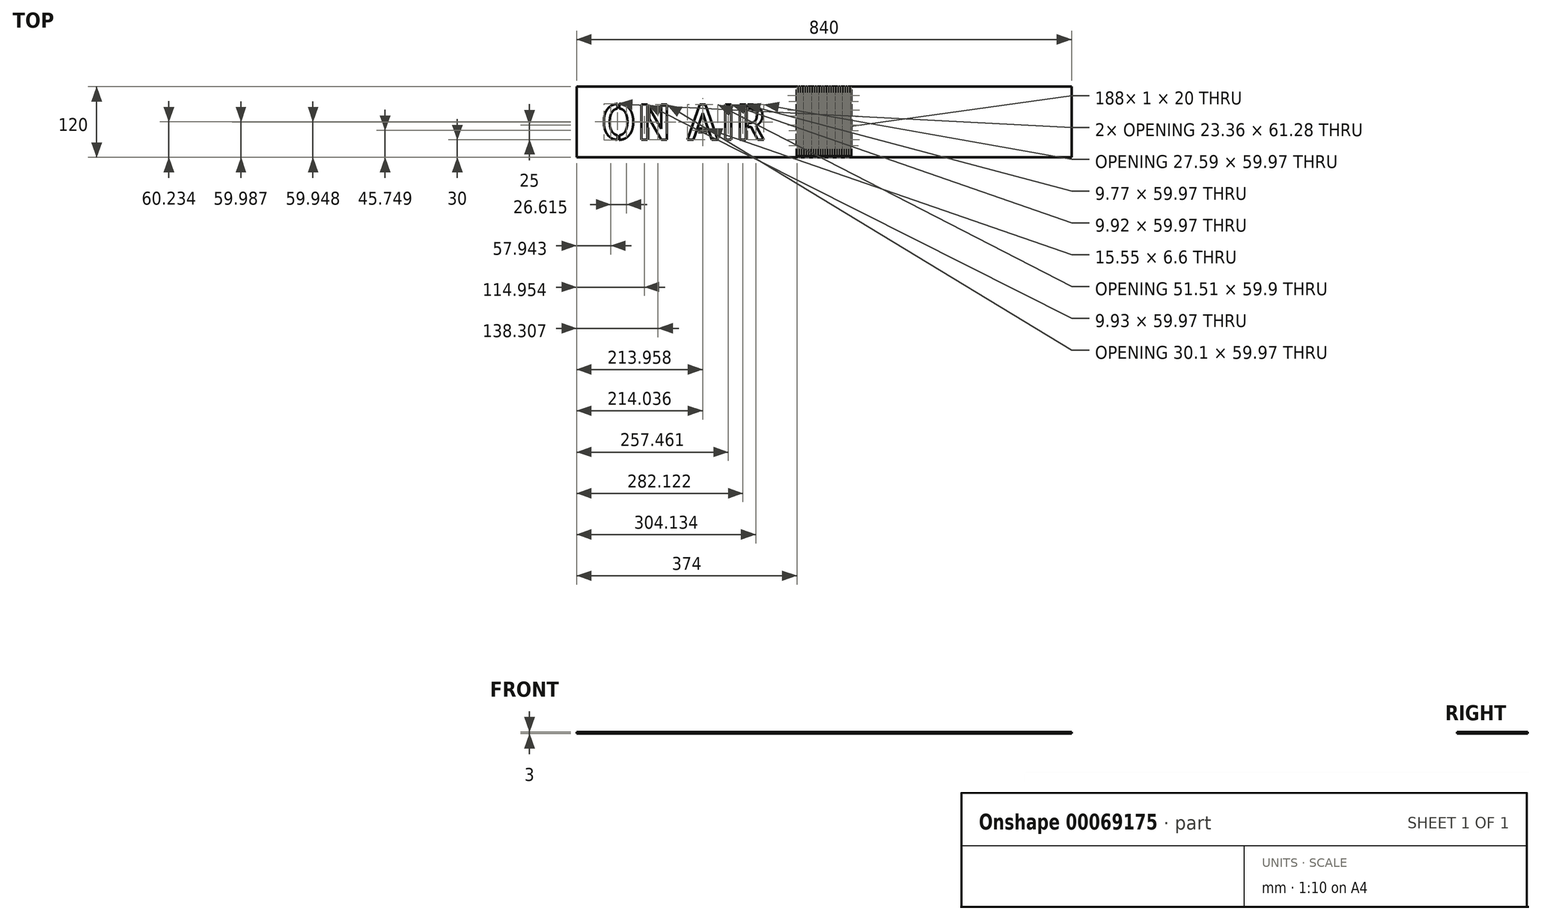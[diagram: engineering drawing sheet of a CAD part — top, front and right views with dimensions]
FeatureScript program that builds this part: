
annotation { "Feature Type Name" : "Feature", "Feature Type Description" : "" }
export const myFeature = defineFeature(function(context is Context, id is Id, definition is map)
    precondition{}
    {
        {
            var Q0;
            Q0=qCreatedBy(makeId("Top.planeOp"),FACE);
            var sketch = newSketch(context, id + "F0", { "sketchPlane" : qUnion([Q0])});
            skLineSegment(sketch, "E0", {"start": v(0, 120) * mm, "end": v(0, 0) * mm});
            skLineSegment(sketch, "E1", {"start": v(0, 0) * mm, "end": v(840, 0) * mm});
            skLineSegment(sketch, "E2", {"start": v(840, 0) * mm, "end": v(840, 120) * mm});
            skLineSegment(sketch, "E3", {"start": v(840, 120) * mm, "end": v(0, 120) * mm});
            skLineSegment(sketch, "E4", {"start": v(420, 120) * mm, "end": v(420, 0) * mm, "construction": true});
            skText(sketch, "E5", { "text": "ON AIR", "fontName": "AllertaStencil-Regular.ttf"});
            skLineSegment(sketch, "E6", {"start": v(417.5, 115) * mm, "end": v(417.5, 95) * mm});
            skLineSegment(sketch, "E7", {"start": v(417.5, 95) * mm, "end": v(418.5, 95) * mm});
            skLineSegment(sketch, "E8", {"start": v(418.5, 95) * mm, "end": v(418.5, 115) * mm});
            skLineSegment(sketch, "E9", {"start": v(418.5, 115) * mm, "end": v(417.5, 115) * mm});
            skLineSegment(sketch, "E10", {"start": v(419.5, 130) * mm, "end": v(419.5, 110) * mm});
            skLineSegment(sketch, "E11", {"start": v(419.5, 110) * mm, "end": v(420.5, 110) * mm});
            skLineSegment(sketch, "E12", {"start": v(420.5, 110) * mm, "end": v(420.5, 130) * mm});
            skLineSegment(sketch, "E13", {"start": v(420.5, 130) * mm, "end": v(419.5, 130) * mm});
            skLineSegment(sketch, "E14", {"start": v(420, 130) * mm, "end": v(420, 110) * mm, "construction": true});
            skPoint(sketch, "E15", {"position": v(419.5, 120) * mm});
            skLineSegment(sketch, "E16.MirrorCS", {"start": v(421.5, 115) * mm, "end": v(422.5, 115) * mm});
            skLineSegment(sketch, "E17.MirrorCS", {"start": v(422.5, 95) * mm, "end": v(421.5, 95) * mm});
            skLineSegment(sketch, "E18.MirrorCS", {"start": v(422.5, 115) * mm, "end": v(422.5, 95) * mm});
            skLineSegment(sketch, "E19.MirrorCS", {"start": v(421.5, 95) * mm, "end": v(421.5, 115) * mm});
            skLineSegment(sketch, "E20.0.1.0", {"start": v(422.5, 90) * mm, "end": v(422.5, 70) * mm});
            skLineSegment(sketch, "E20.0.1.1", {"start": v(418.5, 70) * mm, "end": v(418.5, 90) * mm});
            skLineSegment(sketch, "E20.0.1.2", {"start": v(421.5, 70) * mm, "end": v(421.5, 90) * mm});
            skLineSegment(sketch, "E20.0.1.3", {"start": v(420, 105) * mm, "end": v(420, 85) * mm, "construction": true});
            skLineSegment(sketch, "E20.0.1.4", {"start": v(419.5, 105) * mm, "end": v(419.5, 85) * mm});
            skPoint(sketch, "E20.0.1.5", {"position": v(419.5, 95) * mm});
            skLineSegment(sketch, "E20.0.1.6", {"start": v(420.5, 85) * mm, "end": v(420.5, 105) * mm});
            skLineSegment(sketch, "E20.0.1.7", {"start": v(417.5, 90) * mm, "end": v(417.5, 70) * mm});
            skLineSegment(sketch, "E20.0.1.8", {"start": v(417.5, 70) * mm, "end": v(418.5, 70) * mm});
            skLineSegment(sketch, "E20.0.1.9", {"start": v(420.5, 105) * mm, "end": v(419.5, 105) * mm});
            skLineSegment(sketch, "E20.0.1.10", {"start": v(422.5, 70) * mm, "end": v(421.5, 70) * mm});
            skLineSegment(sketch, "E20.0.1.11", {"start": v(421.5, 90) * mm, "end": v(422.5, 90) * mm});
            skLineSegment(sketch, "E20.0.1.12", {"start": v(418.5, 90) * mm, "end": v(417.5, 90) * mm});
            skLineSegment(sketch, "E20.0.1.13", {"start": v(419.5, 85) * mm, "end": v(420.5, 85) * mm});
            skLineSegment(sketch, "E20.0.2.0", {"start": v(422.5, 65) * mm, "end": v(422.5, 45) * mm});
            skLineSegment(sketch, "E20.0.2.1", {"start": v(418.5, 45) * mm, "end": v(418.5, 65) * mm});
            skLineSegment(sketch, "E20.0.2.2", {"start": v(421.5, 45) * mm, "end": v(421.5, 65) * mm});
            skLineSegment(sketch, "E20.0.2.3", {"start": v(420, 80) * mm, "end": v(420, 60) * mm, "construction": true});
            skLineSegment(sketch, "E20.0.2.4", {"start": v(419.5, 80) * mm, "end": v(419.5, 60) * mm});
            skPoint(sketch, "E20.0.2.5", {"position": v(419.5, 70) * mm});
            skLineSegment(sketch, "E20.0.2.6", {"start": v(420.5, 60) * mm, "end": v(420.5, 80) * mm});
            skLineSegment(sketch, "E20.0.2.7", {"start": v(417.5, 65) * mm, "end": v(417.5, 45) * mm});
            skLineSegment(sketch, "E20.0.2.8", {"start": v(417.5, 45) * mm, "end": v(418.5, 45) * mm});
            skLineSegment(sketch, "E20.0.2.9", {"start": v(420.5, 80) * mm, "end": v(419.5, 80) * mm});
            skLineSegment(sketch, "E20.0.2.10", {"start": v(422.5, 45) * mm, "end": v(421.5, 45) * mm});
            skLineSegment(sketch, "E20.0.2.11", {"start": v(421.5, 65) * mm, "end": v(422.5, 65) * mm});
            skLineSegment(sketch, "E20.0.2.12", {"start": v(418.5, 65) * mm, "end": v(417.5, 65) * mm});
            skLineSegment(sketch, "E20.0.2.13", {"start": v(419.5, 60) * mm, "end": v(420.5, 60) * mm});
            skLineSegment(sketch, "E20.0.3.0", {"start": v(422.5, 40) * mm, "end": v(422.5, 20) * mm});
            skLineSegment(sketch, "E20.0.3.1", {"start": v(418.5, 20) * mm, "end": v(418.5, 40) * mm});
            skLineSegment(sketch, "E20.0.3.2", {"start": v(421.5, 20) * mm, "end": v(421.5, 40) * mm});
            skLineSegment(sketch, "E20.0.3.3", {"start": v(420, 55) * mm, "end": v(420, 35) * mm, "construction": true});
            skLineSegment(sketch, "E20.0.3.4", {"start": v(419.5, 55) * mm, "end": v(419.5, 35) * mm});
            skPoint(sketch, "E20.0.3.5", {"position": v(419.5, 45) * mm});
            skLineSegment(sketch, "E20.0.3.6", {"start": v(420.5, 35) * mm, "end": v(420.5, 55) * mm});
            skLineSegment(sketch, "E20.0.3.7", {"start": v(417.5, 40) * mm, "end": v(417.5, 20) * mm});
            skLineSegment(sketch, "E20.0.3.8", {"start": v(417.5, 20) * mm, "end": v(418.5, 20) * mm});
            skLineSegment(sketch, "E20.0.3.9", {"start": v(420.5, 55) * mm, "end": v(419.5, 55) * mm});
            skLineSegment(sketch, "E20.0.3.10", {"start": v(422.5, 20) * mm, "end": v(421.5, 20) * mm});
            skLineSegment(sketch, "E20.0.3.11", {"start": v(421.5, 40) * mm, "end": v(422.5, 40) * mm});
            skLineSegment(sketch, "E20.0.3.12", {"start": v(418.5, 40) * mm, "end": v(417.5, 40) * mm});
            skLineSegment(sketch, "E20.0.3.13", {"start": v(419.5, 35) * mm, "end": v(420.5, 35) * mm});
            skLineSegment(sketch, "E20.0.4.0", {"start": v(422.5, 15) * mm, "end": v(422.5, -5) * mm});
            skLineSegment(sketch, "E20.0.4.1", {"start": v(418.5, -5) * mm, "end": v(418.5, 15) * mm});
            skLineSegment(sketch, "E20.0.4.2", {"start": v(421.5, -5) * mm, "end": v(421.5, 15) * mm});
            skLineSegment(sketch, "E20.0.4.3", {"start": v(420, 30) * mm, "end": v(420, 10) * mm, "construction": true});
            skLineSegment(sketch, "E20.0.4.4", {"start": v(419.5, 30) * mm, "end": v(419.5, 10) * mm});
            skPoint(sketch, "E20.0.4.5", {"position": v(419.5, 20) * mm});
            skLineSegment(sketch, "E20.0.4.6", {"start": v(420.5, 10) * mm, "end": v(420.5, 30) * mm});
            skLineSegment(sketch, "E20.0.4.7", {"start": v(417.5, 15) * mm, "end": v(417.5, -5) * mm});
            skLineSegment(sketch, "E20.0.4.8", {"start": v(417.5, -5) * mm, "end": v(418.5, -5) * mm});
            skLineSegment(sketch, "E20.0.4.9", {"start": v(420.5, 30) * mm, "end": v(419.5, 30) * mm});
            skLineSegment(sketch, "E20.0.4.10", {"start": v(422.5, -5) * mm, "end": v(421.5, -5) * mm});
            skLineSegment(sketch, "E20.0.4.11", {"start": v(421.5, 15) * mm, "end": v(422.5, 15) * mm});
            skLineSegment(sketch, "E20.0.4.12", {"start": v(418.5, 15) * mm, "end": v(417.5, 15) * mm});
            skLineSegment(sketch, "E20.0.4.13", {"start": v(419.5, 10) * mm, "end": v(420.5, 10) * mm});
            skLineSegment(sketch, "E20.0.5.0", {"start": v(422.5, -10) * mm, "end": v(422.5, -30) * mm});
            skLineSegment(sketch, "E20.0.5.1", {"start": v(418.5, -30) * mm, "end": v(418.5, -10) * mm});
            skLineSegment(sketch, "E20.0.5.2", {"start": v(421.5, -30) * mm, "end": v(421.5, -10) * mm});
            skLineSegment(sketch, "E20.0.5.3", {"start": v(420, 5) * mm, "end": v(420, -15) * mm, "construction": true});
            skLineSegment(sketch, "E20.0.5.4", {"start": v(419.5, 5) * mm, "end": v(419.5, -15) * mm});
            skPoint(sketch, "E20.0.5.5", {"position": v(419.5, -5) * mm});
            skLineSegment(sketch, "E20.0.5.6", {"start": v(420.5, -15) * mm, "end": v(420.5, 5) * mm});
            skLineSegment(sketch, "E20.0.5.7", {"start": v(417.5, -10) * mm, "end": v(417.5, -30) * mm});
            skLineSegment(sketch, "E20.0.5.8", {"start": v(417.5, -30) * mm, "end": v(418.5, -30) * mm});
            skLineSegment(sketch, "E20.0.5.9", {"start": v(420.5, 5) * mm, "end": v(419.5, 5) * mm});
            skLineSegment(sketch, "E20.0.5.10", {"start": v(422.5, -30) * mm, "end": v(421.5, -30) * mm});
            skLineSegment(sketch, "E20.0.5.11", {"start": v(421.5, -10) * mm, "end": v(422.5, -10) * mm});
            skLineSegment(sketch, "E20.0.5.12", {"start": v(418.5, -10) * mm, "end": v(417.5, -10) * mm});
            skLineSegment(sketch, "E20.0.5.13", {"start": v(419.5, -15) * mm, "end": v(420.5, -15) * mm});
            skLineSegment(sketch, "E20.direction1", {"start": v(422.5, 95) * mm, "end": v(422.5, 95) * mm});
            skLineSegment(sketch, "E20.direction2", {"start": v(422.5, 95) * mm, "end": v(422.5, 70) * mm, "construction": true});
            skLineSegment(sketch, "E21.1.0.0", {"start": v(426.5, -10) * mm, "end": v(426.5, -30) * mm});
            skPoint(sketch, "E21.1.0.1", {"position": v(423.5, 95) * mm});
            skLineSegment(sketch, "E21.1.0.2", {"start": v(425.5, 70) * mm, "end": v(425.5, 90) * mm});
            skLineSegment(sketch, "E21.1.0.3", {"start": v(425.5, 45) * mm, "end": v(425.5, 65) * mm});
            skLineSegment(sketch, "E21.1.0.4", {"start": v(426.5, 65) * mm, "end": v(426.5, 45) * mm});
            skPoint(sketch, "E21.1.0.5", {"position": v(423.5, 70) * mm});
            skLineSegment(sketch, "E21.1.0.6", {"start": v(425.5, -5) * mm, "end": v(425.5, 15) * mm});
            skPoint(sketch, "E21.1.0.7", {"position": v(423.5, 20) * mm});
            skLineSegment(sketch, "E21.1.0.8", {"start": v(426.5, 40) * mm, "end": v(426.5, 20) * mm});
            skLineSegment(sketch, "E21.1.0.9", {"start": v(425.5, -30) * mm, "end": v(425.5, -10) * mm});
            skPoint(sketch, "E21.1.0.10", {"position": v(423.5, 45) * mm});
            skLineSegment(sketch, "E21.1.0.11", {"start": v(425.5, 20) * mm, "end": v(425.5, 40) * mm});
            skLineSegment(sketch, "E21.1.0.12", {"start": v(426.5, 90) * mm, "end": v(426.5, 70) * mm});
            skLineSegment(sketch, "E21.1.0.13", {"start": v(426.5, 15) * mm, "end": v(426.5, -5) * mm});
            skPoint(sketch, "E21.1.0.14", {"position": v(423.5, -5) * mm});
            skLineSegment(sketch, "E21.1.0.15", {"start": v(424.5, 85) * mm, "end": v(424.5, 105) * mm});
            skLineSegment(sketch, "E21.1.0.16", {"start": v(426.5, 95) * mm, "end": v(426.5, 70) * mm, "construction": true});
            skLineSegment(sketch, "E21.1.0.17", {"start": v(424.5, 35) * mm, "end": v(424.5, 55) * mm});
            skLineSegment(sketch, "E21.1.0.18", {"start": v(424.5, 60) * mm, "end": v(424.5, 80) * mm});
            skLineSegment(sketch, "E21.1.0.19", {"start": v(424.5, -15) * mm, "end": v(424.5, 5) * mm});
            skLineSegment(sketch, "E21.1.0.20", {"start": v(423.5, 80) * mm, "end": v(423.5, 60) * mm});
            skLineSegment(sketch, "E21.1.0.21", {"start": v(425.5, 15) * mm, "end": v(426.5, 15) * mm});
            skLineSegment(sketch, "E21.1.0.22", {"start": v(423.5, 105) * mm, "end": v(423.5, 85) * mm});
            skLineSegment(sketch, "E21.1.0.23", {"start": v(423.5, 55) * mm, "end": v(423.5, 35) * mm});
            skLineSegment(sketch, "E21.1.0.24", {"start": v(425.5, -10) * mm, "end": v(426.5, -10) * mm});
            skLineSegment(sketch, "E21.1.0.25", {"start": v(424, 55) * mm, "end": v(424, 35) * mm, "construction": true});
            skLineSegment(sketch, "E21.1.0.26", {"start": v(426.5, -5) * mm, "end": v(425.5, -5) * mm});
            skLineSegment(sketch, "E21.1.0.27", {"start": v(423.5, 5) * mm, "end": v(423.5, -15) * mm});
            skLineSegment(sketch, "E21.1.0.28", {"start": v(424, 105) * mm, "end": v(424, 85) * mm, "construction": true});
            skLineSegment(sketch, "E21.1.0.29", {"start": v(424.5, 10) * mm, "end": v(424.5, 30) * mm});
            skLineSegment(sketch, "E21.1.0.30", {"start": v(425.5, 40) * mm, "end": v(426.5, 40) * mm});
            skLineSegment(sketch, "E21.1.0.31", {"start": v(424, 80) * mm, "end": v(424, 60) * mm, "construction": true});
            skLineSegment(sketch, "E21.1.0.32", {"start": v(424, 5) * mm, "end": v(424, -15) * mm, "construction": true});
            skLineSegment(sketch, "E21.1.0.33", {"start": v(426.5, -30) * mm, "end": v(425.5, -30) * mm});
            skLineSegment(sketch, "E21.1.0.34", {"start": v(423.5, 35) * mm, "end": v(424.5, 35) * mm});
            skLineSegment(sketch, "E21.1.0.35", {"start": v(426.5, 20) * mm, "end": v(425.5, 20) * mm});
            skLineSegment(sketch, "E21.1.0.36", {"start": v(426.5, 70) * mm, "end": v(425.5, 70) * mm});
            skLineSegment(sketch, "E21.1.0.37", {"start": v(423.5, -15) * mm, "end": v(424.5, -15) * mm});
            skLineSegment(sketch, "E21.1.0.38", {"start": v(424.5, 30) * mm, "end": v(423.5, 30) * mm});
            skLineSegment(sketch, "E21.1.0.39", {"start": v(424.5, 5) * mm, "end": v(423.5, 5) * mm});
            skLineSegment(sketch, "E21.1.0.40", {"start": v(423.5, 60) * mm, "end": v(424.5, 60) * mm});
            skLineSegment(sketch, "E21.1.0.41", {"start": v(424, 30) * mm, "end": v(424, 10) * mm, "construction": true});
            skLineSegment(sketch, "E21.1.0.42", {"start": v(425.5, 90) * mm, "end": v(426.5, 90) * mm});
            skLineSegment(sketch, "E21.1.0.43", {"start": v(424.5, 80) * mm, "end": v(423.5, 80) * mm});
            skLineSegment(sketch, "E21.1.0.44", {"start": v(423.5, 30) * mm, "end": v(423.5, 10) * mm});
            skLineSegment(sketch, "E21.1.0.45", {"start": v(424.5, 55) * mm, "end": v(423.5, 55) * mm});
            skLineSegment(sketch, "E21.1.0.46", {"start": v(423.5, 85) * mm, "end": v(424.5, 85) * mm});
            skLineSegment(sketch, "E21.1.0.47", {"start": v(423.5, 10) * mm, "end": v(424.5, 10) * mm});
            skLineSegment(sketch, "E21.1.0.48", {"start": v(425.5, 65) * mm, "end": v(426.5, 65) * mm});
            skLineSegment(sketch, "E21.1.0.49", {"start": v(426.5, 45) * mm, "end": v(425.5, 45) * mm});
            skLineSegment(sketch, "E21.1.0.50", {"start": v(425.5, 95) * mm, "end": v(425.5, 115) * mm});
            skLineSegment(sketch, "E21.1.0.51", {"start": v(426.5, 95) * mm, "end": v(425.5, 95) * mm});
            skLineSegment(sketch, "E21.1.0.52", {"start": v(426.5, 115) * mm, "end": v(426.5, 95) * mm});
            skLineSegment(sketch, "E21.1.0.53", {"start": v(425.5, 115) * mm, "end": v(426.5, 115) * mm});
            skLineSegment(sketch, "E21.1.0.54", {"start": v(424.5, 110) * mm, "end": v(424.5, 130) * mm});
            skLineSegment(sketch, "E21.1.0.55", {"start": v(423.5, 130) * mm, "end": v(423.5, 110) * mm});
            skLineSegment(sketch, "E21.1.0.56", {"start": v(423.5, 110) * mm, "end": v(424.5, 110) * mm});
            skLineSegment(sketch, "E21.1.0.57", {"start": v(424.5, 130) * mm, "end": v(423.5, 130) * mm});
            skLineSegment(sketch, "E21.2.0.0", {"start": v(430.5, -10) * mm, "end": v(430.5, -30) * mm});
            skPoint(sketch, "E21.2.0.1", {"position": v(427.5, 95) * mm});
            skLineSegment(sketch, "E21.2.0.2", {"start": v(429.5, 70) * mm, "end": v(429.5, 90) * mm});
            skLineSegment(sketch, "E21.2.0.3", {"start": v(429.5, 45) * mm, "end": v(429.5, 65) * mm});
            skLineSegment(sketch, "E21.2.0.4", {"start": v(430.5, 65) * mm, "end": v(430.5, 45) * mm});
            skPoint(sketch, "E21.2.0.5", {"position": v(427.5, 70) * mm});
            skLineSegment(sketch, "E21.2.0.6", {"start": v(429.5, -5) * mm, "end": v(429.5, 15) * mm});
            skPoint(sketch, "E21.2.0.7", {"position": v(427.5, 20) * mm});
            skLineSegment(sketch, "E21.2.0.8", {"start": v(430.5, 40) * mm, "end": v(430.5, 20) * mm});
            skLineSegment(sketch, "E21.2.0.9", {"start": v(429.5, -30) * mm, "end": v(429.5, -10) * mm});
            skPoint(sketch, "E21.2.0.10", {"position": v(427.5, 45) * mm});
            skLineSegment(sketch, "E21.2.0.11", {"start": v(429.5, 20) * mm, "end": v(429.5, 40) * mm});
            skLineSegment(sketch, "E21.2.0.12", {"start": v(430.5, 90) * mm, "end": v(430.5, 70) * mm});
            skLineSegment(sketch, "E21.2.0.13", {"start": v(430.5, 15) * mm, "end": v(430.5, -5) * mm});
            skPoint(sketch, "E21.2.0.14", {"position": v(427.5, -5) * mm});
            skLineSegment(sketch, "E21.2.0.15", {"start": v(428.5, 85) * mm, "end": v(428.5, 105) * mm});
            skLineSegment(sketch, "E21.2.0.16", {"start": v(430.5, 95) * mm, "end": v(430.5, 70) * mm, "construction": true});
            skLineSegment(sketch, "E21.2.0.17", {"start": v(428.5, 35) * mm, "end": v(428.5, 55) * mm});
            skLineSegment(sketch, "E21.2.0.18", {"start": v(428.5, 60) * mm, "end": v(428.5, 80) * mm});
            skLineSegment(sketch, "E21.2.0.19", {"start": v(428.5, -15) * mm, "end": v(428.5, 5) * mm});
            skLineSegment(sketch, "E21.2.0.20", {"start": v(427.5, 80) * mm, "end": v(427.5, 60) * mm});
            skLineSegment(sketch, "E21.2.0.21", {"start": v(429.5, 15) * mm, "end": v(430.5, 15) * mm});
            skLineSegment(sketch, "E21.2.0.22", {"start": v(427.5, 105) * mm, "end": v(427.5, 85) * mm});
            skLineSegment(sketch, "E21.2.0.23", {"start": v(427.5, 55) * mm, "end": v(427.5, 35) * mm});
            skLineSegment(sketch, "E21.2.0.24", {"start": v(429.5, -10) * mm, "end": v(430.5, -10) * mm});
            skLineSegment(sketch, "E21.2.0.25", {"start": v(428, 55) * mm, "end": v(428, 35) * mm, "construction": true});
            skLineSegment(sketch, "E21.2.0.26", {"start": v(430.5, -5) * mm, "end": v(429.5, -5) * mm});
            skLineSegment(sketch, "E21.2.0.27", {"start": v(427.5, 5) * mm, "end": v(427.5, -15) * mm});
            skLineSegment(sketch, "E21.2.0.28", {"start": v(428, 105) * mm, "end": v(428, 85) * mm, "construction": true});
            skLineSegment(sketch, "E21.2.0.29", {"start": v(428.5, 10) * mm, "end": v(428.5, 30) * mm});
            skLineSegment(sketch, "E21.2.0.30", {"start": v(429.5, 40) * mm, "end": v(430.5, 40) * mm});
            skLineSegment(sketch, "E21.2.0.31", {"start": v(428, 80) * mm, "end": v(428, 60) * mm, "construction": true});
            skLineSegment(sketch, "E21.2.0.32", {"start": v(428, 5) * mm, "end": v(428, -15) * mm, "construction": true});
            skLineSegment(sketch, "E21.2.0.33", {"start": v(430.5, -30) * mm, "end": v(429.5, -30) * mm});
            skLineSegment(sketch, "E21.2.0.34", {"start": v(427.5, 35) * mm, "end": v(428.5, 35) * mm});
            skLineSegment(sketch, "E21.2.0.35", {"start": v(430.5, 20) * mm, "end": v(429.5, 20) * mm});
            skLineSegment(sketch, "E21.2.0.36", {"start": v(430.5, 70) * mm, "end": v(429.5, 70) * mm});
            skLineSegment(sketch, "E21.2.0.37", {"start": v(427.5, -15) * mm, "end": v(428.5, -15) * mm});
            skLineSegment(sketch, "E21.2.0.38", {"start": v(428.5, 30) * mm, "end": v(427.5, 30) * mm});
            skLineSegment(sketch, "E21.2.0.39", {"start": v(428.5, 5) * mm, "end": v(427.5, 5) * mm});
            skLineSegment(sketch, "E21.2.0.40", {"start": v(427.5, 60) * mm, "end": v(428.5, 60) * mm});
            skLineSegment(sketch, "E21.2.0.41", {"start": v(428, 30) * mm, "end": v(428, 10) * mm, "construction": true});
            skLineSegment(sketch, "E21.2.0.42", {"start": v(429.5, 90) * mm, "end": v(430.5, 90) * mm});
            skLineSegment(sketch, "E21.2.0.43", {"start": v(428.5, 80) * mm, "end": v(427.5, 80) * mm});
            skLineSegment(sketch, "E21.2.0.44", {"start": v(427.5, 30) * mm, "end": v(427.5, 10) * mm});
            skLineSegment(sketch, "E21.2.0.45", {"start": v(428.5, 55) * mm, "end": v(427.5, 55) * mm});
            skLineSegment(sketch, "E21.2.0.46", {"start": v(427.5, 85) * mm, "end": v(428.5, 85) * mm});
            skLineSegment(sketch, "E21.2.0.47", {"start": v(427.5, 10) * mm, "end": v(428.5, 10) * mm});
            skLineSegment(sketch, "E21.2.0.48", {"start": v(429.5, 65) * mm, "end": v(430.5, 65) * mm});
            skLineSegment(sketch, "E21.2.0.49", {"start": v(430.5, 45) * mm, "end": v(429.5, 45) * mm});
            skLineSegment(sketch, "E21.2.0.50", {"start": v(429.5, 95) * mm, "end": v(429.5, 115) * mm});
            skLineSegment(sketch, "E21.2.0.51", {"start": v(430.5, 95) * mm, "end": v(429.5, 95) * mm});
            skLineSegment(sketch, "E21.2.0.52", {"start": v(430.5, 115) * mm, "end": v(430.5, 95) * mm});
            skLineSegment(sketch, "E21.2.0.53", {"start": v(429.5, 115) * mm, "end": v(430.5, 115) * mm});
            skLineSegment(sketch, "E21.2.0.54", {"start": v(428.5, 110) * mm, "end": v(428.5, 130) * mm});
            skLineSegment(sketch, "E21.2.0.55", {"start": v(427.5, 130) * mm, "end": v(427.5, 110) * mm});
            skLineSegment(sketch, "E21.2.0.56", {"start": v(427.5, 110) * mm, "end": v(428.5, 110) * mm});
            skLineSegment(sketch, "E21.2.0.57", {"start": v(428.5, 130) * mm, "end": v(427.5, 130) * mm});
            skLineSegment(sketch, "E21.3.0.0", {"start": v(434.5, -10) * mm, "end": v(434.5, -30) * mm});
            skPoint(sketch, "E21.3.0.1", {"position": v(431.5, 95) * mm});
            skLineSegment(sketch, "E21.3.0.2", {"start": v(433.5, 70) * mm, "end": v(433.5, 90) * mm});
            skLineSegment(sketch, "E21.3.0.3", {"start": v(433.5, 45) * mm, "end": v(433.5, 65) * mm});
            skLineSegment(sketch, "E21.3.0.4", {"start": v(434.5, 65) * mm, "end": v(434.5, 45) * mm});
            skPoint(sketch, "E21.3.0.5", {"position": v(431.5, 70) * mm});
            skLineSegment(sketch, "E21.3.0.6", {"start": v(433.5, -5) * mm, "end": v(433.5, 15) * mm});
            skPoint(sketch, "E21.3.0.7", {"position": v(431.5, 20) * mm});
            skLineSegment(sketch, "E21.3.0.8", {"start": v(434.5, 40) * mm, "end": v(434.5, 20) * mm});
            skLineSegment(sketch, "E21.3.0.9", {"start": v(433.5, -30) * mm, "end": v(433.5, -10) * mm});
            skPoint(sketch, "E21.3.0.10", {"position": v(431.5, 45) * mm});
            skLineSegment(sketch, "E21.3.0.11", {"start": v(433.5, 20) * mm, "end": v(433.5, 40) * mm});
            skLineSegment(sketch, "E21.3.0.12", {"start": v(434.5, 90) * mm, "end": v(434.5, 70) * mm});
            skLineSegment(sketch, "E21.3.0.13", {"start": v(434.5, 15) * mm, "end": v(434.5, -5) * mm});
            skPoint(sketch, "E21.3.0.14", {"position": v(431.5, -5) * mm});
            skLineSegment(sketch, "E21.3.0.15", {"start": v(432.5, 85) * mm, "end": v(432.5, 105) * mm});
            skLineSegment(sketch, "E21.3.0.16", {"start": v(434.5, 95) * mm, "end": v(434.5, 70) * mm, "construction": true});
            skLineSegment(sketch, "E21.3.0.17", {"start": v(432.5, 35) * mm, "end": v(432.5, 55) * mm});
            skLineSegment(sketch, "E21.3.0.18", {"start": v(432.5, 60) * mm, "end": v(432.5, 80) * mm});
            skLineSegment(sketch, "E21.3.0.19", {"start": v(432.5, -15) * mm, "end": v(432.5, 5) * mm});
            skLineSegment(sketch, "E21.3.0.20", {"start": v(431.5, 80) * mm, "end": v(431.5, 60) * mm});
            skLineSegment(sketch, "E21.3.0.21", {"start": v(433.5, 15) * mm, "end": v(434.5, 15) * mm});
            skLineSegment(sketch, "E21.3.0.22", {"start": v(431.5, 105) * mm, "end": v(431.5, 85) * mm});
            skLineSegment(sketch, "E21.3.0.23", {"start": v(431.5, 55) * mm, "end": v(431.5, 35) * mm});
            skLineSegment(sketch, "E21.3.0.24", {"start": v(433.5, -10) * mm, "end": v(434.5, -10) * mm});
            skLineSegment(sketch, "E21.3.0.25", {"start": v(432, 55) * mm, "end": v(432, 35) * mm, "construction": true});
            skLineSegment(sketch, "E21.3.0.26", {"start": v(434.5, -5) * mm, "end": v(433.5, -5) * mm});
            skLineSegment(sketch, "E21.3.0.27", {"start": v(431.5, 5) * mm, "end": v(431.5, -15) * mm});
            skLineSegment(sketch, "E21.3.0.28", {"start": v(432, 105) * mm, "end": v(432, 85) * mm, "construction": true});
            skLineSegment(sketch, "E21.3.0.29", {"start": v(432.5, 10) * mm, "end": v(432.5, 30) * mm});
            skLineSegment(sketch, "E21.3.0.30", {"start": v(433.5, 40) * mm, "end": v(434.5, 40) * mm});
            skLineSegment(sketch, "E21.3.0.31", {"start": v(432, 80) * mm, "end": v(432, 60) * mm, "construction": true});
            skLineSegment(sketch, "E21.3.0.32", {"start": v(432, 5) * mm, "end": v(432, -15) * mm, "construction": true});
            skLineSegment(sketch, "E21.3.0.33", {"start": v(434.5, -30) * mm, "end": v(433.5, -30) * mm});
            skLineSegment(sketch, "E21.3.0.34", {"start": v(431.5, 35) * mm, "end": v(432.5, 35) * mm});
            skLineSegment(sketch, "E21.3.0.35", {"start": v(434.5, 20) * mm, "end": v(433.5, 20) * mm});
            skLineSegment(sketch, "E21.3.0.36", {"start": v(434.5, 70) * mm, "end": v(433.5, 70) * mm});
            skLineSegment(sketch, "E21.3.0.37", {"start": v(431.5, -15) * mm, "end": v(432.5, -15) * mm});
            skLineSegment(sketch, "E21.3.0.38", {"start": v(432.5, 30) * mm, "end": v(431.5, 30) * mm});
            skLineSegment(sketch, "E21.3.0.39", {"start": v(432.5, 5) * mm, "end": v(431.5, 5) * mm});
            skLineSegment(sketch, "E21.3.0.40", {"start": v(431.5, 60) * mm, "end": v(432.5, 60) * mm});
            skLineSegment(sketch, "E21.3.0.41", {"start": v(432, 30) * mm, "end": v(432, 10) * mm, "construction": true});
            skLineSegment(sketch, "E21.3.0.42", {"start": v(433.5, 90) * mm, "end": v(434.5, 90) * mm});
            skLineSegment(sketch, "E21.3.0.43", {"start": v(432.5, 80) * mm, "end": v(431.5, 80) * mm});
            skLineSegment(sketch, "E21.3.0.44", {"start": v(431.5, 30) * mm, "end": v(431.5, 10) * mm});
            skLineSegment(sketch, "E21.3.0.45", {"start": v(432.5, 55) * mm, "end": v(431.5, 55) * mm});
            skLineSegment(sketch, "E21.3.0.46", {"start": v(431.5, 85) * mm, "end": v(432.5, 85) * mm});
            skLineSegment(sketch, "E21.3.0.47", {"start": v(431.5, 10) * mm, "end": v(432.5, 10) * mm});
            skLineSegment(sketch, "E21.3.0.48", {"start": v(433.5, 65) * mm, "end": v(434.5, 65) * mm});
            skLineSegment(sketch, "E21.3.0.49", {"start": v(434.5, 45) * mm, "end": v(433.5, 45) * mm});
            skLineSegment(sketch, "E21.3.0.50", {"start": v(433.5, 95) * mm, "end": v(433.5, 115) * mm});
            skLineSegment(sketch, "E21.3.0.51", {"start": v(434.5, 95) * mm, "end": v(433.5, 95) * mm});
            skLineSegment(sketch, "E21.3.0.52", {"start": v(434.5, 115) * mm, "end": v(434.5, 95) * mm});
            skLineSegment(sketch, "E21.3.0.53", {"start": v(433.5, 115) * mm, "end": v(434.5, 115) * mm});
            skLineSegment(sketch, "E21.3.0.54", {"start": v(432.5, 110) * mm, "end": v(432.5, 130) * mm});
            skLineSegment(sketch, "E21.3.0.55", {"start": v(431.5, 130) * mm, "end": v(431.5, 110) * mm});
            skLineSegment(sketch, "E21.3.0.56", {"start": v(431.5, 110) * mm, "end": v(432.5, 110) * mm});
            skLineSegment(sketch, "E21.3.0.57", {"start": v(432.5, 130) * mm, "end": v(431.5, 130) * mm});
            skLineSegment(sketch, "E21.4.0.0", {"start": v(438.5, -10) * mm, "end": v(438.5, -30) * mm});
            skPoint(sketch, "E21.4.0.1", {"position": v(435.5, 95) * mm});
            skLineSegment(sketch, "E21.4.0.2", {"start": v(437.5, 70) * mm, "end": v(437.5, 90) * mm});
            skLineSegment(sketch, "E21.4.0.3", {"start": v(437.5, 45) * mm, "end": v(437.5, 65) * mm});
            skLineSegment(sketch, "E21.4.0.4", {"start": v(438.5, 65) * mm, "end": v(438.5, 45) * mm});
            skPoint(sketch, "E21.4.0.5", {"position": v(435.5, 70) * mm});
            skLineSegment(sketch, "E21.4.0.6", {"start": v(437.5, -5) * mm, "end": v(437.5, 15) * mm});
            skPoint(sketch, "E21.4.0.7", {"position": v(435.5, 20) * mm});
            skLineSegment(sketch, "E21.4.0.8", {"start": v(438.5, 40) * mm, "end": v(438.5, 20) * mm});
            skLineSegment(sketch, "E21.4.0.9", {"start": v(437.5, -30) * mm, "end": v(437.5, -10) * mm});
            skPoint(sketch, "E21.4.0.10", {"position": v(435.5, 45) * mm});
            skLineSegment(sketch, "E21.4.0.11", {"start": v(437.5, 20) * mm, "end": v(437.5, 40) * mm});
            skLineSegment(sketch, "E21.4.0.12", {"start": v(438.5, 90) * mm, "end": v(438.5, 70) * mm});
            skLineSegment(sketch, "E21.4.0.13", {"start": v(438.5, 15) * mm, "end": v(438.5, -5) * mm});
            skPoint(sketch, "E21.4.0.14", {"position": v(435.5, -5) * mm});
            skLineSegment(sketch, "E21.4.0.15", {"start": v(436.5, 85) * mm, "end": v(436.5, 105) * mm});
            skLineSegment(sketch, "E21.4.0.16", {"start": v(438.5, 95) * mm, "end": v(438.5, 70) * mm, "construction": true});
            skLineSegment(sketch, "E21.4.0.17", {"start": v(436.5, 35) * mm, "end": v(436.5, 55) * mm});
            skLineSegment(sketch, "E21.4.0.18", {"start": v(436.5, 60) * mm, "end": v(436.5, 80) * mm});
            skLineSegment(sketch, "E21.4.0.19", {"start": v(436.5, -15) * mm, "end": v(436.5, 5) * mm});
            skLineSegment(sketch, "E21.4.0.20", {"start": v(435.5, 80) * mm, "end": v(435.5, 60) * mm});
            skLineSegment(sketch, "E21.4.0.21", {"start": v(437.5, 15) * mm, "end": v(438.5, 15) * mm});
            skLineSegment(sketch, "E21.4.0.22", {"start": v(435.5, 105) * mm, "end": v(435.5, 85) * mm});
            skLineSegment(sketch, "E21.4.0.23", {"start": v(435.5, 55) * mm, "end": v(435.5, 35) * mm});
            skLineSegment(sketch, "E21.4.0.24", {"start": v(437.5, -10) * mm, "end": v(438.5, -10) * mm});
            skLineSegment(sketch, "E21.4.0.25", {"start": v(436, 55) * mm, "end": v(436, 35) * mm, "construction": true});
            skLineSegment(sketch, "E21.4.0.26", {"start": v(438.5, -5) * mm, "end": v(437.5, -5) * mm});
            skLineSegment(sketch, "E21.4.0.27", {"start": v(435.5, 5) * mm, "end": v(435.5, -15) * mm});
            skLineSegment(sketch, "E21.4.0.28", {"start": v(436, 105) * mm, "end": v(436, 85) * mm, "construction": true});
            skLineSegment(sketch, "E21.4.0.29", {"start": v(436.5, 10) * mm, "end": v(436.5, 30) * mm});
            skLineSegment(sketch, "E21.4.0.30", {"start": v(437.5, 40) * mm, "end": v(438.5, 40) * mm});
            skLineSegment(sketch, "E21.4.0.31", {"start": v(436, 80) * mm, "end": v(436, 60) * mm, "construction": true});
            skLineSegment(sketch, "E21.4.0.32", {"start": v(436, 5) * mm, "end": v(436, -15) * mm, "construction": true});
            skLineSegment(sketch, "E21.4.0.33", {"start": v(438.5, -30) * mm, "end": v(437.5, -30) * mm});
            skLineSegment(sketch, "E21.4.0.34", {"start": v(435.5, 35) * mm, "end": v(436.5, 35) * mm});
            skLineSegment(sketch, "E21.4.0.35", {"start": v(438.5, 20) * mm, "end": v(437.5, 20) * mm});
            skLineSegment(sketch, "E21.4.0.36", {"start": v(438.5, 70) * mm, "end": v(437.5, 70) * mm});
            skLineSegment(sketch, "E21.4.0.37", {"start": v(435.5, -15) * mm, "end": v(436.5, -15) * mm});
            skLineSegment(sketch, "E21.4.0.38", {"start": v(436.5, 30) * mm, "end": v(435.5, 30) * mm});
            skLineSegment(sketch, "E21.4.0.39", {"start": v(436.5, 5) * mm, "end": v(435.5, 5) * mm});
            skLineSegment(sketch, "E21.4.0.40", {"start": v(435.5, 60) * mm, "end": v(436.5, 60) * mm});
            skLineSegment(sketch, "E21.4.0.41", {"start": v(436, 30) * mm, "end": v(436, 10) * mm, "construction": true});
            skLineSegment(sketch, "E21.4.0.42", {"start": v(437.5, 90) * mm, "end": v(438.5, 90) * mm});
            skLineSegment(sketch, "E21.4.0.43", {"start": v(436.5, 80) * mm, "end": v(435.5, 80) * mm});
            skLineSegment(sketch, "E21.4.0.44", {"start": v(435.5, 30) * mm, "end": v(435.5, 10) * mm});
            skLineSegment(sketch, "E21.4.0.45", {"start": v(436.5, 55) * mm, "end": v(435.5, 55) * mm});
            skLineSegment(sketch, "E21.4.0.46", {"start": v(435.5, 85) * mm, "end": v(436.5, 85) * mm});
            skLineSegment(sketch, "E21.4.0.47", {"start": v(435.5, 10) * mm, "end": v(436.5, 10) * mm});
            skLineSegment(sketch, "E21.4.0.48", {"start": v(437.5, 65) * mm, "end": v(438.5, 65) * mm});
            skLineSegment(sketch, "E21.4.0.49", {"start": v(438.5, 45) * mm, "end": v(437.5, 45) * mm});
            skLineSegment(sketch, "E21.4.0.50", {"start": v(437.5, 95) * mm, "end": v(437.5, 115) * mm});
            skLineSegment(sketch, "E21.4.0.51", {"start": v(438.5, 95) * mm, "end": v(437.5, 95) * mm});
            skLineSegment(sketch, "E21.4.0.52", {"start": v(438.5, 115) * mm, "end": v(438.5, 95) * mm});
            skLineSegment(sketch, "E21.4.0.53", {"start": v(437.5, 115) * mm, "end": v(438.5, 115) * mm});
            skLineSegment(sketch, "E21.4.0.54", {"start": v(436.5, 110) * mm, "end": v(436.5, 130) * mm});
            skLineSegment(sketch, "E21.4.0.55", {"start": v(435.5, 130) * mm, "end": v(435.5, 110) * mm});
            skLineSegment(sketch, "E21.4.0.56", {"start": v(435.5, 110) * mm, "end": v(436.5, 110) * mm});
            skLineSegment(sketch, "E21.4.0.57", {"start": v(436.5, 130) * mm, "end": v(435.5, 130) * mm});
            skLineSegment(sketch, "E21.5.0.0", {"start": v(442.5, -10) * mm, "end": v(442.5, -30) * mm});
            skPoint(sketch, "E21.5.0.1", {"position": v(439.5, 95) * mm});
            skLineSegment(sketch, "E21.5.0.2", {"start": v(441.5, 70) * mm, "end": v(441.5, 90) * mm});
            skLineSegment(sketch, "E21.5.0.3", {"start": v(441.5, 45) * mm, "end": v(441.5, 65) * mm});
            skLineSegment(sketch, "E21.5.0.4", {"start": v(442.5, 65) * mm, "end": v(442.5, 45) * mm});
            skPoint(sketch, "E21.5.0.5", {"position": v(439.5, 70) * mm});
            skLineSegment(sketch, "E21.5.0.6", {"start": v(441.5, -5) * mm, "end": v(441.5, 15) * mm});
            skPoint(sketch, "E21.5.0.7", {"position": v(439.5, 20) * mm});
            skLineSegment(sketch, "E21.5.0.8", {"start": v(442.5, 40) * mm, "end": v(442.5, 20) * mm});
            skLineSegment(sketch, "E21.5.0.9", {"start": v(441.5, -30) * mm, "end": v(441.5, -10) * mm});
            skPoint(sketch, "E21.5.0.10", {"position": v(439.5, 45) * mm});
            skLineSegment(sketch, "E21.5.0.11", {"start": v(441.5, 20) * mm, "end": v(441.5, 40) * mm});
            skLineSegment(sketch, "E21.5.0.12", {"start": v(442.5, 90) * mm, "end": v(442.5, 70) * mm});
            skLineSegment(sketch, "E21.5.0.13", {"start": v(442.5, 15) * mm, "end": v(442.5, -5) * mm});
            skPoint(sketch, "E21.5.0.14", {"position": v(439.5, -5) * mm});
            skLineSegment(sketch, "E21.5.0.15", {"start": v(440.5, 85) * mm, "end": v(440.5, 105) * mm});
            skLineSegment(sketch, "E21.5.0.16", {"start": v(442.5, 95) * mm, "end": v(442.5, 70) * mm, "construction": true});
            skLineSegment(sketch, "E21.5.0.17", {"start": v(440.5, 35) * mm, "end": v(440.5, 55) * mm});
            skLineSegment(sketch, "E21.5.0.18", {"start": v(440.5, 60) * mm, "end": v(440.5, 80) * mm});
            skLineSegment(sketch, "E21.5.0.19", {"start": v(440.5, -15) * mm, "end": v(440.5, 5) * mm});
            skLineSegment(sketch, "E21.5.0.20", {"start": v(439.5, 80) * mm, "end": v(439.5, 60) * mm});
            skLineSegment(sketch, "E21.5.0.21", {"start": v(441.5, 15) * mm, "end": v(442.5, 15) * mm});
            skLineSegment(sketch, "E21.5.0.22", {"start": v(439.5, 105) * mm, "end": v(439.5, 85) * mm});
            skLineSegment(sketch, "E21.5.0.23", {"start": v(439.5, 55) * mm, "end": v(439.5, 35) * mm});
            skLineSegment(sketch, "E21.5.0.24", {"start": v(441.5, -10) * mm, "end": v(442.5, -10) * mm});
            skLineSegment(sketch, "E21.5.0.25", {"start": v(440, 55) * mm, "end": v(440, 35) * mm, "construction": true});
            skLineSegment(sketch, "E21.5.0.26", {"start": v(442.5, -5) * mm, "end": v(441.5, -5) * mm});
            skLineSegment(sketch, "E21.5.0.27", {"start": v(439.5, 5) * mm, "end": v(439.5, -15) * mm});
            skLineSegment(sketch, "E21.5.0.28", {"start": v(440, 105) * mm, "end": v(440, 85) * mm, "construction": true});
            skLineSegment(sketch, "E21.5.0.29", {"start": v(440.5, 10) * mm, "end": v(440.5, 30) * mm});
            skLineSegment(sketch, "E21.5.0.30", {"start": v(441.5, 40) * mm, "end": v(442.5, 40) * mm});
            skLineSegment(sketch, "E21.5.0.31", {"start": v(440, 80) * mm, "end": v(440, 60) * mm, "construction": true});
            skLineSegment(sketch, "E21.5.0.32", {"start": v(440, 5) * mm, "end": v(440, -15) * mm, "construction": true});
            skLineSegment(sketch, "E21.5.0.33", {"start": v(442.5, -30) * mm, "end": v(441.5, -30) * mm});
            skLineSegment(sketch, "E21.5.0.34", {"start": v(439.5, 35) * mm, "end": v(440.5, 35) * mm});
            skLineSegment(sketch, "E21.5.0.35", {"start": v(442.5, 20) * mm, "end": v(441.5, 20) * mm});
            skLineSegment(sketch, "E21.5.0.36", {"start": v(442.5, 70) * mm, "end": v(441.5, 70) * mm});
            skLineSegment(sketch, "E21.5.0.37", {"start": v(439.5, -15) * mm, "end": v(440.5, -15) * mm});
            skLineSegment(sketch, "E21.5.0.38", {"start": v(440.5, 30) * mm, "end": v(439.5, 30) * mm});
            skLineSegment(sketch, "E21.5.0.39", {"start": v(440.5, 5) * mm, "end": v(439.5, 5) * mm});
            skLineSegment(sketch, "E21.5.0.40", {"start": v(439.5, 60) * mm, "end": v(440.5, 60) * mm});
            skLineSegment(sketch, "E21.5.0.41", {"start": v(440, 30) * mm, "end": v(440, 10) * mm, "construction": true});
            skLineSegment(sketch, "E21.5.0.42", {"start": v(441.5, 90) * mm, "end": v(442.5, 90) * mm});
            skLineSegment(sketch, "E21.5.0.43", {"start": v(440.5, 80) * mm, "end": v(439.5, 80) * mm});
            skLineSegment(sketch, "E21.5.0.44", {"start": v(439.5, 30) * mm, "end": v(439.5, 10) * mm});
            skLineSegment(sketch, "E21.5.0.45", {"start": v(440.5, 55) * mm, "end": v(439.5, 55) * mm});
            skLineSegment(sketch, "E21.5.0.46", {"start": v(439.5, 85) * mm, "end": v(440.5, 85) * mm});
            skLineSegment(sketch, "E21.5.0.47", {"start": v(439.5, 10) * mm, "end": v(440.5, 10) * mm});
            skLineSegment(sketch, "E21.5.0.48", {"start": v(441.5, 65) * mm, "end": v(442.5, 65) * mm});
            skLineSegment(sketch, "E21.5.0.49", {"start": v(442.5, 45) * mm, "end": v(441.5, 45) * mm});
            skLineSegment(sketch, "E21.5.0.50", {"start": v(441.5, 95) * mm, "end": v(441.5, 115) * mm});
            skLineSegment(sketch, "E21.5.0.51", {"start": v(442.5, 95) * mm, "end": v(441.5, 95) * mm});
            skLineSegment(sketch, "E21.5.0.52", {"start": v(442.5, 115) * mm, "end": v(442.5, 95) * mm});
            skLineSegment(sketch, "E21.5.0.53", {"start": v(441.5, 115) * mm, "end": v(442.5, 115) * mm});
            skLineSegment(sketch, "E21.5.0.54", {"start": v(440.5, 110) * mm, "end": v(440.5, 130) * mm});
            skLineSegment(sketch, "E21.5.0.55", {"start": v(439.5, 130) * mm, "end": v(439.5, 110) * mm});
            skLineSegment(sketch, "E21.5.0.56", {"start": v(439.5, 110) * mm, "end": v(440.5, 110) * mm});
            skLineSegment(sketch, "E21.5.0.57", {"start": v(440.5, 130) * mm, "end": v(439.5, 130) * mm});
            skLineSegment(sketch, "E21.6.0.0", {"start": v(446.5, -10) * mm, "end": v(446.5, -30) * mm});
            skPoint(sketch, "E21.6.0.1", {"position": v(443.5, 95) * mm});
            skLineSegment(sketch, "E21.6.0.2", {"start": v(445.5, 70) * mm, "end": v(445.5, 90) * mm});
            skLineSegment(sketch, "E21.6.0.3", {"start": v(445.5, 45) * mm, "end": v(445.5, 65) * mm});
            skLineSegment(sketch, "E21.6.0.4", {"start": v(446.5, 65) * mm, "end": v(446.5, 45) * mm});
            skPoint(sketch, "E21.6.0.5", {"position": v(443.5, 70) * mm});
            skLineSegment(sketch, "E21.6.0.6", {"start": v(445.5, -5) * mm, "end": v(445.5, 15) * mm});
            skPoint(sketch, "E21.6.0.7", {"position": v(443.5, 20) * mm});
            skLineSegment(sketch, "E21.6.0.8", {"start": v(446.5, 40) * mm, "end": v(446.5, 20) * mm});
            skLineSegment(sketch, "E21.6.0.9", {"start": v(445.5, -30) * mm, "end": v(445.5, -10) * mm});
            skPoint(sketch, "E21.6.0.10", {"position": v(443.5, 45) * mm});
            skLineSegment(sketch, "E21.6.0.11", {"start": v(445.5, 20) * mm, "end": v(445.5, 40) * mm});
            skLineSegment(sketch, "E21.6.0.12", {"start": v(446.5, 90) * mm, "end": v(446.5, 70) * mm});
            skLineSegment(sketch, "E21.6.0.13", {"start": v(446.5, 15) * mm, "end": v(446.5, -5) * mm});
            skPoint(sketch, "E21.6.0.14", {"position": v(443.5, -5) * mm});
            skLineSegment(sketch, "E21.6.0.15", {"start": v(444.5, 85) * mm, "end": v(444.5, 105) * mm});
            skLineSegment(sketch, "E21.6.0.16", {"start": v(446.5, 95) * mm, "end": v(446.5, 70) * mm, "construction": true});
            skLineSegment(sketch, "E21.6.0.17", {"start": v(444.5, 35) * mm, "end": v(444.5, 55) * mm});
            skLineSegment(sketch, "E21.6.0.18", {"start": v(444.5, 60) * mm, "end": v(444.5, 80) * mm});
            skLineSegment(sketch, "E21.6.0.19", {"start": v(444.5, -15) * mm, "end": v(444.5, 5) * mm});
            skLineSegment(sketch, "E21.6.0.20", {"start": v(443.5, 80) * mm, "end": v(443.5, 60) * mm});
            skLineSegment(sketch, "E21.6.0.21", {"start": v(445.5, 15) * mm, "end": v(446.5, 15) * mm});
            skLineSegment(sketch, "E21.6.0.22", {"start": v(443.5, 105) * mm, "end": v(443.5, 85) * mm});
            skLineSegment(sketch, "E21.6.0.23", {"start": v(443.5, 55) * mm, "end": v(443.5, 35) * mm});
            skLineSegment(sketch, "E21.6.0.24", {"start": v(445.5, -10) * mm, "end": v(446.5, -10) * mm});
            skLineSegment(sketch, "E21.6.0.25", {"start": v(444, 55) * mm, "end": v(444, 35) * mm, "construction": true});
            skLineSegment(sketch, "E21.6.0.26", {"start": v(446.5, -5) * mm, "end": v(445.5, -5) * mm});
            skLineSegment(sketch, "E21.6.0.27", {"start": v(443.5, 5) * mm, "end": v(443.5, -15) * mm});
            skLineSegment(sketch, "E21.6.0.28", {"start": v(444, 105) * mm, "end": v(444, 85) * mm, "construction": true});
            skLineSegment(sketch, "E21.6.0.29", {"start": v(444.5, 10) * mm, "end": v(444.5, 30) * mm});
            skLineSegment(sketch, "E21.6.0.30", {"start": v(445.5, 40) * mm, "end": v(446.5, 40) * mm});
            skLineSegment(sketch, "E21.6.0.31", {"start": v(444, 80) * mm, "end": v(444, 60) * mm, "construction": true});
            skLineSegment(sketch, "E21.6.0.32", {"start": v(444, 5) * mm, "end": v(444, -15) * mm, "construction": true});
            skLineSegment(sketch, "E21.6.0.33", {"start": v(446.5, -30) * mm, "end": v(445.5, -30) * mm});
            skLineSegment(sketch, "E21.6.0.34", {"start": v(443.5, 35) * mm, "end": v(444.5, 35) * mm});
            skLineSegment(sketch, "E21.6.0.35", {"start": v(446.5, 20) * mm, "end": v(445.5, 20) * mm});
            skLineSegment(sketch, "E21.6.0.36", {"start": v(446.5, 70) * mm, "end": v(445.5, 70) * mm});
            skLineSegment(sketch, "E21.6.0.37", {"start": v(443.5, -15) * mm, "end": v(444.5, -15) * mm});
            skLineSegment(sketch, "E21.6.0.38", {"start": v(444.5, 30) * mm, "end": v(443.5, 30) * mm});
            skLineSegment(sketch, "E21.6.0.39", {"start": v(444.5, 5) * mm, "end": v(443.5, 5) * mm});
            skLineSegment(sketch, "E21.6.0.40", {"start": v(443.5, 60) * mm, "end": v(444.5, 60) * mm});
            skLineSegment(sketch, "E21.6.0.41", {"start": v(444, 30) * mm, "end": v(444, 10) * mm, "construction": true});
            skLineSegment(sketch, "E21.6.0.42", {"start": v(445.5, 90) * mm, "end": v(446.5, 90) * mm});
            skLineSegment(sketch, "E21.6.0.43", {"start": v(444.5, 80) * mm, "end": v(443.5, 80) * mm});
            skLineSegment(sketch, "E21.6.0.44", {"start": v(443.5, 30) * mm, "end": v(443.5, 10) * mm});
            skLineSegment(sketch, "E21.6.0.45", {"start": v(444.5, 55) * mm, "end": v(443.5, 55) * mm});
            skLineSegment(sketch, "E21.6.0.46", {"start": v(443.5, 85) * mm, "end": v(444.5, 85) * mm});
            skLineSegment(sketch, "E21.6.0.47", {"start": v(443.5, 10) * mm, "end": v(444.5, 10) * mm});
            skLineSegment(sketch, "E21.6.0.48", {"start": v(445.5, 65) * mm, "end": v(446.5, 65) * mm});
            skLineSegment(sketch, "E21.6.0.49", {"start": v(446.5, 45) * mm, "end": v(445.5, 45) * mm});
            skLineSegment(sketch, "E21.6.0.50", {"start": v(445.5, 95) * mm, "end": v(445.5, 115) * mm});
            skLineSegment(sketch, "E21.6.0.51", {"start": v(446.5, 95) * mm, "end": v(445.5, 95) * mm});
            skLineSegment(sketch, "E21.6.0.52", {"start": v(446.5, 115) * mm, "end": v(446.5, 95) * mm});
            skLineSegment(sketch, "E21.6.0.53", {"start": v(445.5, 115) * mm, "end": v(446.5, 115) * mm});
            skLineSegment(sketch, "E21.6.0.54", {"start": v(444.5, 110) * mm, "end": v(444.5, 130) * mm});
            skLineSegment(sketch, "E21.6.0.55", {"start": v(443.5, 130) * mm, "end": v(443.5, 110) * mm});
            skLineSegment(sketch, "E21.6.0.56", {"start": v(443.5, 110) * mm, "end": v(444.5, 110) * mm});
            skLineSegment(sketch, "E21.6.0.57", {"start": v(444.5, 130) * mm, "end": v(443.5, 130) * mm});
            skLineSegment(sketch, "E21.7.0.0", {"start": v(450.5, -10) * mm, "end": v(450.5, -30) * mm});
            skPoint(sketch, "E21.7.0.1", {"position": v(447.5, 95) * mm});
            skLineSegment(sketch, "E21.7.0.2", {"start": v(449.5, 70) * mm, "end": v(449.5, 90) * mm});
            skLineSegment(sketch, "E21.7.0.3", {"start": v(449.5, 45) * mm, "end": v(449.5, 65) * mm});
            skLineSegment(sketch, "E21.7.0.4", {"start": v(450.5, 65) * mm, "end": v(450.5, 45) * mm});
            skPoint(sketch, "E21.7.0.5", {"position": v(447.5, 70) * mm});
            skLineSegment(sketch, "E21.7.0.6", {"start": v(449.5, -5) * mm, "end": v(449.5, 15) * mm});
            skPoint(sketch, "E21.7.0.7", {"position": v(447.5, 20) * mm});
            skLineSegment(sketch, "E21.7.0.8", {"start": v(450.5, 40) * mm, "end": v(450.5, 20) * mm});
            skLineSegment(sketch, "E21.7.0.9", {"start": v(449.5, -30) * mm, "end": v(449.5, -10) * mm});
            skPoint(sketch, "E21.7.0.10", {"position": v(447.5, 45) * mm});
            skLineSegment(sketch, "E21.7.0.11", {"start": v(449.5, 20) * mm, "end": v(449.5, 40) * mm});
            skLineSegment(sketch, "E21.7.0.12", {"start": v(450.5, 90) * mm, "end": v(450.5, 70) * mm});
            skLineSegment(sketch, "E21.7.0.13", {"start": v(450.5, 15) * mm, "end": v(450.5, -5) * mm});
            skPoint(sketch, "E21.7.0.14", {"position": v(447.5, -5) * mm});
            skLineSegment(sketch, "E21.7.0.15", {"start": v(448.5, 85) * mm, "end": v(448.5, 105) * mm});
            skLineSegment(sketch, "E21.7.0.16", {"start": v(450.5, 95) * mm, "end": v(450.5, 70) * mm, "construction": true});
            skLineSegment(sketch, "E21.7.0.17", {"start": v(448.5, 35) * mm, "end": v(448.5, 55) * mm});
            skLineSegment(sketch, "E21.7.0.18", {"start": v(448.5, 60) * mm, "end": v(448.5, 80) * mm});
            skLineSegment(sketch, "E21.7.0.19", {"start": v(448.5, -15) * mm, "end": v(448.5, 5) * mm});
            skLineSegment(sketch, "E21.7.0.20", {"start": v(447.5, 80) * mm, "end": v(447.5, 60) * mm});
            skLineSegment(sketch, "E21.7.0.21", {"start": v(449.5, 15) * mm, "end": v(450.5, 15) * mm});
            skLineSegment(sketch, "E21.7.0.22", {"start": v(447.5, 105) * mm, "end": v(447.5, 85) * mm});
            skLineSegment(sketch, "E21.7.0.23", {"start": v(447.5, 55) * mm, "end": v(447.5, 35) * mm});
            skLineSegment(sketch, "E21.7.0.24", {"start": v(449.5, -10) * mm, "end": v(450.5, -10) * mm});
            skLineSegment(sketch, "E21.7.0.25", {"start": v(448, 55) * mm, "end": v(448, 35) * mm, "construction": true});
            skLineSegment(sketch, "E21.7.0.26", {"start": v(450.5, -5) * mm, "end": v(449.5, -5) * mm});
            skLineSegment(sketch, "E21.7.0.27", {"start": v(447.5, 5) * mm, "end": v(447.5, -15) * mm});
            skLineSegment(sketch, "E21.7.0.28", {"start": v(448, 105) * mm, "end": v(448, 85) * mm, "construction": true});
            skLineSegment(sketch, "E21.7.0.29", {"start": v(448.5, 10) * mm, "end": v(448.5, 30) * mm});
            skLineSegment(sketch, "E21.7.0.30", {"start": v(449.5, 40) * mm, "end": v(450.5, 40) * mm});
            skLineSegment(sketch, "E21.7.0.31", {"start": v(448, 80) * mm, "end": v(448, 60) * mm, "construction": true});
            skLineSegment(sketch, "E21.7.0.32", {"start": v(448, 5) * mm, "end": v(448, -15) * mm, "construction": true});
            skLineSegment(sketch, "E21.7.0.33", {"start": v(450.5, -30) * mm, "end": v(449.5, -30) * mm});
            skLineSegment(sketch, "E21.7.0.34", {"start": v(447.5, 35) * mm, "end": v(448.5, 35) * mm});
            skLineSegment(sketch, "E21.7.0.35", {"start": v(450.5, 20) * mm, "end": v(449.5, 20) * mm});
            skLineSegment(sketch, "E21.7.0.36", {"start": v(450.5, 70) * mm, "end": v(449.5, 70) * mm});
            skLineSegment(sketch, "E21.7.0.37", {"start": v(447.5, -15) * mm, "end": v(448.5, -15) * mm});
            skLineSegment(sketch, "E21.7.0.38", {"start": v(448.5, 30) * mm, "end": v(447.5, 30) * mm});
            skLineSegment(sketch, "E21.7.0.39", {"start": v(448.5, 5) * mm, "end": v(447.5, 5) * mm});
            skLineSegment(sketch, "E21.7.0.40", {"start": v(447.5, 60) * mm, "end": v(448.5, 60) * mm});
            skLineSegment(sketch, "E21.7.0.41", {"start": v(448, 30) * mm, "end": v(448, 10) * mm, "construction": true});
            skLineSegment(sketch, "E21.7.0.42", {"start": v(449.5, 90) * mm, "end": v(450.5, 90) * mm});
            skLineSegment(sketch, "E21.7.0.43", {"start": v(448.5, 80) * mm, "end": v(447.5, 80) * mm});
            skLineSegment(sketch, "E21.7.0.44", {"start": v(447.5, 30) * mm, "end": v(447.5, 10) * mm});
            skLineSegment(sketch, "E21.7.0.45", {"start": v(448.5, 55) * mm, "end": v(447.5, 55) * mm});
            skLineSegment(sketch, "E21.7.0.46", {"start": v(447.5, 85) * mm, "end": v(448.5, 85) * mm});
            skLineSegment(sketch, "E21.7.0.47", {"start": v(447.5, 10) * mm, "end": v(448.5, 10) * mm});
            skLineSegment(sketch, "E21.7.0.48", {"start": v(449.5, 65) * mm, "end": v(450.5, 65) * mm});
            skLineSegment(sketch, "E21.7.0.49", {"start": v(450.5, 45) * mm, "end": v(449.5, 45) * mm});
            skLineSegment(sketch, "E21.7.0.50", {"start": v(449.5, 95) * mm, "end": v(449.5, 115) * mm});
            skLineSegment(sketch, "E21.7.0.51", {"start": v(450.5, 95) * mm, "end": v(449.5, 95) * mm});
            skLineSegment(sketch, "E21.7.0.52", {"start": v(450.5, 115) * mm, "end": v(450.5, 95) * mm});
            skLineSegment(sketch, "E21.7.0.53", {"start": v(449.5, 115) * mm, "end": v(450.5, 115) * mm});
            skLineSegment(sketch, "E21.7.0.54", {"start": v(448.5, 110) * mm, "end": v(448.5, 130) * mm});
            skLineSegment(sketch, "E21.7.0.55", {"start": v(447.5, 130) * mm, "end": v(447.5, 110) * mm});
            skLineSegment(sketch, "E21.7.0.56", {"start": v(447.5, 110) * mm, "end": v(448.5, 110) * mm});
            skLineSegment(sketch, "E21.7.0.57", {"start": v(448.5, 130) * mm, "end": v(447.5, 130) * mm});
            skLineSegment(sketch, "E21.direction1", {"start": v(422.5, -30) * mm, "end": v(426.5, -30) * mm, "construction": true});
            skLineSegment(sketch, "E22.1.0.0", {"start": v(413.5, 90) * mm, "end": v(413.5, 70) * mm});
            skLineSegment(sketch, "E22.1.0.1", {"start": v(413.5, 115) * mm, "end": v(413.5, 95) * mm});
            skLineSegment(sketch, "E22.1.0.2", {"start": v(413.5, 65) * mm, "end": v(413.5, 45) * mm});
            skLineSegment(sketch, "E22.1.0.3", {"start": v(414.5, 70) * mm, "end": v(414.5, 90) * mm});
            skLineSegment(sketch, "E22.1.0.4", {"start": v(413.5, 15) * mm, "end": v(413.5, -5) * mm});
            skPoint(sketch, "E22.1.0.5", {"position": v(415.5, 70) * mm});
            skPoint(sketch, "E22.1.0.6", {"position": v(415.5, 120) * mm});
            skPoint(sketch, "E22.1.0.7", {"position": v(415.5, 20) * mm});
            skLineSegment(sketch, "E22.1.0.8", {"start": v(414.5, 45) * mm, "end": v(414.5, 65) * mm});
            skPoint(sketch, "E22.1.0.9", {"position": v(415.5, 95) * mm});
            skLineSegment(sketch, "E22.1.0.10", {"start": v(413.5, 40) * mm, "end": v(413.5, 20) * mm});
            skLineSegment(sketch, "E22.1.0.11", {"start": v(416.5, 110) * mm, "end": v(416.5, 130) * mm});
            skLineSegment(sketch, "E22.1.0.12", {"start": v(415.5, 130) * mm, "end": v(415.5, 110) * mm});
            skLineSegment(sketch, "E22.1.0.13", {"start": v(413.5, -10) * mm, "end": v(413.5, -30) * mm});
            skLineSegment(sketch, "E22.1.0.14", {"start": v(414.5, -5) * mm, "end": v(414.5, 15) * mm});
            skLineSegment(sketch, "E22.1.0.15", {"start": v(414.5, 95) * mm, "end": v(414.5, 115) * mm});
            skPoint(sketch, "E22.1.0.16", {"position": v(415.5, 45) * mm});
            skLineSegment(sketch, "E22.1.0.17", {"start": v(414.5, -30) * mm, "end": v(414.5, -10) * mm});
            skPoint(sketch, "E22.1.0.18", {"position": v(415.5, -5) * mm});
            skLineSegment(sketch, "E22.1.0.19", {"start": v(414.5, 20) * mm, "end": v(414.5, 40) * mm});
            skLineSegment(sketch, "E22.1.0.20", {"start": v(415.5, 105) * mm, "end": v(415.5, 85) * mm});
            skLineSegment(sketch, "E22.1.0.21", {"start": v(416.5, 60) * mm, "end": v(416.5, 80) * mm});
            skLineSegment(sketch, "E22.1.0.22", {"start": v(415.5, 80) * mm, "end": v(415.5, 60) * mm});
            skLineSegment(sketch, "E22.1.0.23", {"start": v(416.5, -15) * mm, "end": v(416.5, 5) * mm});
            skLineSegment(sketch, "E22.1.0.24", {"start": v(415.5, 5) * mm, "end": v(415.5, -15) * mm});
            skLineSegment(sketch, "E22.1.0.25", {"start": v(416.5, 85) * mm, "end": v(416.5, 105) * mm});
            skLineSegment(sketch, "E22.1.0.26", {"start": v(416, 130) * mm, "end": v(416, 110) * mm, "construction": true});
            skLineSegment(sketch, "E22.1.0.27", {"start": v(416, 105) * mm, "end": v(416, 85) * mm, "construction": true});
            skLineSegment(sketch, "E22.1.0.28", {"start": v(416.5, 10) * mm, "end": v(416.5, 30) * mm});
            skLineSegment(sketch, "E22.1.0.29", {"start": v(415.5, 55) * mm, "end": v(415.5, 35) * mm});
            skLineSegment(sketch, "E22.1.0.30", {"start": v(416, 80) * mm, "end": v(416, 60) * mm, "construction": true});
            skLineSegment(sketch, "E22.1.0.31", {"start": v(416, 5) * mm, "end": v(416, -15) * mm, "construction": true});
            skLineSegment(sketch, "E22.1.0.32", {"start": v(416.5, 35) * mm, "end": v(416.5, 55) * mm});
            skLineSegment(sketch, "E22.1.0.33", {"start": v(415.5, 30) * mm, "end": v(415.5, 10) * mm});
            skLineSegment(sketch, "E22.1.0.34", {"start": v(416.5, 80) * mm, "end": v(415.5, 80) * mm});
            skLineSegment(sketch, "E22.1.0.35", {"start": v(416, 30) * mm, "end": v(416, 10) * mm, "construction": true});
            skLineSegment(sketch, "E22.1.0.36", {"start": v(416, 55) * mm, "end": v(416, 35) * mm, "construction": true});
            skLineSegment(sketch, "E22.1.0.37", {"start": v(416.5, 5) * mm, "end": v(415.5, 5) * mm});
            skLineSegment(sketch, "E22.1.0.38", {"start": v(415.5, 85) * mm, "end": v(416.5, 85) * mm});
            skLineSegment(sketch, "E22.1.0.39", {"start": v(415.5, -15) * mm, "end": v(416.5, -15) * mm});
            skLineSegment(sketch, "E22.1.0.40", {"start": v(416.5, 105) * mm, "end": v(415.5, 105) * mm});
            skLineSegment(sketch, "E22.1.0.41", {"start": v(414.5, 115) * mm, "end": v(413.5, 115) * mm});
            skLineSegment(sketch, "E22.1.0.42", {"start": v(415.5, 35) * mm, "end": v(416.5, 35) * mm});
            skLineSegment(sketch, "E22.1.0.43", {"start": v(415.5, 10) * mm, "end": v(416.5, 10) * mm});
            skLineSegment(sketch, "E22.1.0.44", {"start": v(414.5, 15) * mm, "end": v(413.5, 15) * mm});
            skLineSegment(sketch, "E22.1.0.45", {"start": v(416.5, 55) * mm, "end": v(415.5, 55) * mm});
            skLineSegment(sketch, "E22.1.0.46", {"start": v(413.5, 20) * mm, "end": v(414.5, 20) * mm});
            skLineSegment(sketch, "E22.1.0.47", {"start": v(413.5, -5) * mm, "end": v(414.5, -5) * mm});
            skLineSegment(sketch, "E22.1.0.48", {"start": v(414.5, 90) * mm, "end": v(413.5, 90) * mm});
            skLineSegment(sketch, "E22.1.0.49", {"start": v(413.5, -30) * mm, "end": v(414.5, -30) * mm});
            skLineSegment(sketch, "E22.1.0.50", {"start": v(415.5, 60) * mm, "end": v(416.5, 60) * mm});
            skLineSegment(sketch, "E22.1.0.51", {"start": v(415.5, 110) * mm, "end": v(416.5, 110) * mm});
            skLineSegment(sketch, "E22.1.0.52", {"start": v(414.5, -10) * mm, "end": v(413.5, -10) * mm});
            skLineSegment(sketch, "E22.1.0.53", {"start": v(413.5, 45) * mm, "end": v(414.5, 45) * mm});
            skLineSegment(sketch, "E22.1.0.54", {"start": v(413.5, 95) * mm, "end": v(414.5, 95) * mm});
            skLineSegment(sketch, "E22.1.0.55", {"start": v(416.5, 30) * mm, "end": v(415.5, 30) * mm});
            skLineSegment(sketch, "E22.1.0.56", {"start": v(414.5, 40) * mm, "end": v(413.5, 40) * mm});
            skLineSegment(sketch, "E22.1.0.57", {"start": v(413.5, 70) * mm, "end": v(414.5, 70) * mm});
            skLineSegment(sketch, "E22.1.0.58", {"start": v(414.5, 65) * mm, "end": v(413.5, 65) * mm});
            skLineSegment(sketch, "E22.1.0.59", {"start": v(416.5, 130) * mm, "end": v(415.5, 130) * mm});
            skLineSegment(sketch, "E22.2.0.0", {"start": v(409.5, 90) * mm, "end": v(409.5, 70) * mm});
            skLineSegment(sketch, "E22.2.0.1", {"start": v(409.5, 115) * mm, "end": v(409.5, 95) * mm});
            skLineSegment(sketch, "E22.2.0.2", {"start": v(409.5, 65) * mm, "end": v(409.5, 45) * mm});
            skLineSegment(sketch, "E22.2.0.3", {"start": v(410.5, 70) * mm, "end": v(410.5, 90) * mm});
            skLineSegment(sketch, "E22.2.0.4", {"start": v(409.5, 15) * mm, "end": v(409.5, -5) * mm});
            skPoint(sketch, "E22.2.0.5", {"position": v(411.5, 70) * mm});
            skPoint(sketch, "E22.2.0.6", {"position": v(411.5, 120) * mm});
            skPoint(sketch, "E22.2.0.7", {"position": v(411.5, 20) * mm});
            skLineSegment(sketch, "E22.2.0.8", {"start": v(410.5, 45) * mm, "end": v(410.5, 65) * mm});
            skPoint(sketch, "E22.2.0.9", {"position": v(411.5, 95) * mm});
            skLineSegment(sketch, "E22.2.0.10", {"start": v(409.5, 40) * mm, "end": v(409.5, 20) * mm});
            skLineSegment(sketch, "E22.2.0.11", {"start": v(412.5, 110) * mm, "end": v(412.5, 130) * mm});
            skLineSegment(sketch, "E22.2.0.12", {"start": v(411.5, 130) * mm, "end": v(411.5, 110) * mm});
            skLineSegment(sketch, "E22.2.0.13", {"start": v(409.5, -10) * mm, "end": v(409.5, -30) * mm});
            skLineSegment(sketch, "E22.2.0.14", {"start": v(410.5, -5) * mm, "end": v(410.5, 15) * mm});
            skLineSegment(sketch, "E22.2.0.15", {"start": v(410.5, 95) * mm, "end": v(410.5, 115) * mm});
            skPoint(sketch, "E22.2.0.16", {"position": v(411.5, 45) * mm});
            skLineSegment(sketch, "E22.2.0.17", {"start": v(410.5, -30) * mm, "end": v(410.5, -10) * mm});
            skPoint(sketch, "E22.2.0.18", {"position": v(411.5, -5) * mm});
            skLineSegment(sketch, "E22.2.0.19", {"start": v(410.5, 20) * mm, "end": v(410.5, 40) * mm});
            skLineSegment(sketch, "E22.2.0.20", {"start": v(411.5, 105) * mm, "end": v(411.5, 85) * mm});
            skLineSegment(sketch, "E22.2.0.21", {"start": v(412.5, 60) * mm, "end": v(412.5, 80) * mm});
            skLineSegment(sketch, "E22.2.0.22", {"start": v(411.5, 80) * mm, "end": v(411.5, 60) * mm});
            skLineSegment(sketch, "E22.2.0.23", {"start": v(412.5, -15) * mm, "end": v(412.5, 5) * mm});
            skLineSegment(sketch, "E22.2.0.24", {"start": v(411.5, 5) * mm, "end": v(411.5, -15) * mm});
            skLineSegment(sketch, "E22.2.0.25", {"start": v(412.5, 85) * mm, "end": v(412.5, 105) * mm});
            skLineSegment(sketch, "E22.2.0.26", {"start": v(412, 130) * mm, "end": v(412, 110) * mm, "construction": true});
            skLineSegment(sketch, "E22.2.0.27", {"start": v(412, 105) * mm, "end": v(412, 85) * mm, "construction": true});
            skLineSegment(sketch, "E22.2.0.28", {"start": v(412.5, 10) * mm, "end": v(412.5, 30) * mm});
            skLineSegment(sketch, "E22.2.0.29", {"start": v(411.5, 55) * mm, "end": v(411.5, 35) * mm});
            skLineSegment(sketch, "E22.2.0.30", {"start": v(412, 80) * mm, "end": v(412, 60) * mm, "construction": true});
            skLineSegment(sketch, "E22.2.0.31", {"start": v(412, 5) * mm, "end": v(412, -15) * mm, "construction": true});
            skLineSegment(sketch, "E22.2.0.32", {"start": v(412.5, 35) * mm, "end": v(412.5, 55) * mm});
            skLineSegment(sketch, "E22.2.0.33", {"start": v(411.5, 30) * mm, "end": v(411.5, 10) * mm});
            skLineSegment(sketch, "E22.2.0.34", {"start": v(412.5, 80) * mm, "end": v(411.5, 80) * mm});
            skLineSegment(sketch, "E22.2.0.35", {"start": v(412, 30) * mm, "end": v(412, 10) * mm, "construction": true});
            skLineSegment(sketch, "E22.2.0.36", {"start": v(412, 55) * mm, "end": v(412, 35) * mm, "construction": true});
            skLineSegment(sketch, "E22.2.0.37", {"start": v(412.5, 5) * mm, "end": v(411.5, 5) * mm});
            skLineSegment(sketch, "E22.2.0.38", {"start": v(411.5, 85) * mm, "end": v(412.5, 85) * mm});
            skLineSegment(sketch, "E22.2.0.39", {"start": v(411.5, -15) * mm, "end": v(412.5, -15) * mm});
            skLineSegment(sketch, "E22.2.0.40", {"start": v(412.5, 105) * mm, "end": v(411.5, 105) * mm});
            skLineSegment(sketch, "E22.2.0.41", {"start": v(410.5, 115) * mm, "end": v(409.5, 115) * mm});
            skLineSegment(sketch, "E22.2.0.42", {"start": v(411.5, 35) * mm, "end": v(412.5, 35) * mm});
            skLineSegment(sketch, "E22.2.0.43", {"start": v(411.5, 10) * mm, "end": v(412.5, 10) * mm});
            skLineSegment(sketch, "E22.2.0.44", {"start": v(410.5, 15) * mm, "end": v(409.5, 15) * mm});
            skLineSegment(sketch, "E22.2.0.45", {"start": v(412.5, 55) * mm, "end": v(411.5, 55) * mm});
            skLineSegment(sketch, "E22.2.0.46", {"start": v(409.5, 20) * mm, "end": v(410.5, 20) * mm});
            skLineSegment(sketch, "E22.2.0.47", {"start": v(409.5, -5) * mm, "end": v(410.5, -5) * mm});
            skLineSegment(sketch, "E22.2.0.48", {"start": v(410.5, 90) * mm, "end": v(409.5, 90) * mm});
            skLineSegment(sketch, "E22.2.0.49", {"start": v(409.5, -30) * mm, "end": v(410.5, -30) * mm});
            skLineSegment(sketch, "E22.2.0.50", {"start": v(411.5, 60) * mm, "end": v(412.5, 60) * mm});
            skLineSegment(sketch, "E22.2.0.51", {"start": v(411.5, 110) * mm, "end": v(412.5, 110) * mm});
            skLineSegment(sketch, "E22.2.0.52", {"start": v(410.5, -10) * mm, "end": v(409.5, -10) * mm});
            skLineSegment(sketch, "E22.2.0.53", {"start": v(409.5, 45) * mm, "end": v(410.5, 45) * mm});
            skLineSegment(sketch, "E22.2.0.54", {"start": v(409.5, 95) * mm, "end": v(410.5, 95) * mm});
            skLineSegment(sketch, "E22.2.0.55", {"start": v(412.5, 30) * mm, "end": v(411.5, 30) * mm});
            skLineSegment(sketch, "E22.2.0.56", {"start": v(410.5, 40) * mm, "end": v(409.5, 40) * mm});
            skLineSegment(sketch, "E22.2.0.57", {"start": v(409.5, 70) * mm, "end": v(410.5, 70) * mm});
            skLineSegment(sketch, "E22.2.0.58", {"start": v(410.5, 65) * mm, "end": v(409.5, 65) * mm});
            skLineSegment(sketch, "E22.2.0.59", {"start": v(412.5, 130) * mm, "end": v(411.5, 130) * mm});
            skLineSegment(sketch, "E22.3.0.0", {"start": v(405.5, 90) * mm, "end": v(405.5, 70) * mm});
            skLineSegment(sketch, "E22.3.0.1", {"start": v(405.5, 115) * mm, "end": v(405.5, 95) * mm});
            skLineSegment(sketch, "E22.3.0.2", {"start": v(405.5, 65) * mm, "end": v(405.5, 45) * mm});
            skLineSegment(sketch, "E22.3.0.3", {"start": v(406.5, 70) * mm, "end": v(406.5, 90) * mm});
            skLineSegment(sketch, "E22.3.0.4", {"start": v(405.5, 15) * mm, "end": v(405.5, -5) * mm});
            skPoint(sketch, "E22.3.0.5", {"position": v(407.5, 70) * mm});
            skPoint(sketch, "E22.3.0.6", {"position": v(407.5, 120) * mm});
            skPoint(sketch, "E22.3.0.7", {"position": v(407.5, 20) * mm});
            skLineSegment(sketch, "E22.3.0.8", {"start": v(406.5, 45) * mm, "end": v(406.5, 65) * mm});
            skPoint(sketch, "E22.3.0.9", {"position": v(407.5, 95) * mm});
            skLineSegment(sketch, "E22.3.0.10", {"start": v(405.5, 40) * mm, "end": v(405.5, 20) * mm});
            skLineSegment(sketch, "E22.3.0.11", {"start": v(408.5, 110) * mm, "end": v(408.5, 130) * mm});
            skLineSegment(sketch, "E22.3.0.12", {"start": v(407.5, 130) * mm, "end": v(407.5, 110) * mm});
            skLineSegment(sketch, "E22.3.0.13", {"start": v(405.5, -10) * mm, "end": v(405.5, -30) * mm});
            skLineSegment(sketch, "E22.3.0.14", {"start": v(406.5, -5) * mm, "end": v(406.5, 15) * mm});
            skLineSegment(sketch, "E22.3.0.15", {"start": v(406.5, 95) * mm, "end": v(406.5, 115) * mm});
            skPoint(sketch, "E22.3.0.16", {"position": v(407.5, 45) * mm});
            skLineSegment(sketch, "E22.3.0.17", {"start": v(406.5, -30) * mm, "end": v(406.5, -10) * mm});
            skPoint(sketch, "E22.3.0.18", {"position": v(407.5, -5) * mm});
            skLineSegment(sketch, "E22.3.0.19", {"start": v(406.5, 20) * mm, "end": v(406.5, 40) * mm});
            skLineSegment(sketch, "E22.3.0.20", {"start": v(407.5, 105) * mm, "end": v(407.5, 85) * mm});
            skLineSegment(sketch, "E22.3.0.21", {"start": v(408.5, 60) * mm, "end": v(408.5, 80) * mm});
            skLineSegment(sketch, "E22.3.0.22", {"start": v(407.5, 80) * mm, "end": v(407.5, 60) * mm});
            skLineSegment(sketch, "E22.3.0.23", {"start": v(408.5, -15) * mm, "end": v(408.5, 5) * mm});
            skLineSegment(sketch, "E22.3.0.24", {"start": v(407.5, 5) * mm, "end": v(407.5, -15) * mm});
            skLineSegment(sketch, "E22.3.0.25", {"start": v(408.5, 85) * mm, "end": v(408.5, 105) * mm});
            skLineSegment(sketch, "E22.3.0.26", {"start": v(408, 130) * mm, "end": v(408, 110) * mm, "construction": true});
            skLineSegment(sketch, "E22.3.0.27", {"start": v(408, 105) * mm, "end": v(408, 85) * mm, "construction": true});
            skLineSegment(sketch, "E22.3.0.28", {"start": v(408.5, 10) * mm, "end": v(408.5, 30) * mm});
            skLineSegment(sketch, "E22.3.0.29", {"start": v(407.5, 55) * mm, "end": v(407.5, 35) * mm});
            skLineSegment(sketch, "E22.3.0.30", {"start": v(408, 80) * mm, "end": v(408, 60) * mm, "construction": true});
            skLineSegment(sketch, "E22.3.0.31", {"start": v(408, 5) * mm, "end": v(408, -15) * mm, "construction": true});
            skLineSegment(sketch, "E22.3.0.32", {"start": v(408.5, 35) * mm, "end": v(408.5, 55) * mm});
            skLineSegment(sketch, "E22.3.0.33", {"start": v(407.5, 30) * mm, "end": v(407.5, 10) * mm});
            skLineSegment(sketch, "E22.3.0.34", {"start": v(408.5, 80) * mm, "end": v(407.5, 80) * mm});
            skLineSegment(sketch, "E22.3.0.35", {"start": v(408, 30) * mm, "end": v(408, 10) * mm, "construction": true});
            skLineSegment(sketch, "E22.3.0.36", {"start": v(408, 55) * mm, "end": v(408, 35) * mm, "construction": true});
            skLineSegment(sketch, "E22.3.0.37", {"start": v(408.5, 5) * mm, "end": v(407.5, 5) * mm});
            skLineSegment(sketch, "E22.3.0.38", {"start": v(407.5, 85) * mm, "end": v(408.5, 85) * mm});
            skLineSegment(sketch, "E22.3.0.39", {"start": v(407.5, -15) * mm, "end": v(408.5, -15) * mm});
            skLineSegment(sketch, "E22.3.0.40", {"start": v(408.5, 105) * mm, "end": v(407.5, 105) * mm});
            skLineSegment(sketch, "E22.3.0.41", {"start": v(406.5, 115) * mm, "end": v(405.5, 115) * mm});
            skLineSegment(sketch, "E22.3.0.42", {"start": v(407.5, 35) * mm, "end": v(408.5, 35) * mm});
            skLineSegment(sketch, "E22.3.0.43", {"start": v(407.5, 10) * mm, "end": v(408.5, 10) * mm});
            skLineSegment(sketch, "E22.3.0.44", {"start": v(406.5, 15) * mm, "end": v(405.5, 15) * mm});
            skLineSegment(sketch, "E22.3.0.45", {"start": v(408.5, 55) * mm, "end": v(407.5, 55) * mm});
            skLineSegment(sketch, "E22.3.0.46", {"start": v(405.5, 20) * mm, "end": v(406.5, 20) * mm});
            skLineSegment(sketch, "E22.3.0.47", {"start": v(405.5, -5) * mm, "end": v(406.5, -5) * mm});
            skLineSegment(sketch, "E22.3.0.48", {"start": v(406.5, 90) * mm, "end": v(405.5, 90) * mm});
            skLineSegment(sketch, "E22.3.0.49", {"start": v(405.5, -30) * mm, "end": v(406.5, -30) * mm});
            skLineSegment(sketch, "E22.3.0.50", {"start": v(407.5, 60) * mm, "end": v(408.5, 60) * mm});
            skLineSegment(sketch, "E22.3.0.51", {"start": v(407.5, 110) * mm, "end": v(408.5, 110) * mm});
            skLineSegment(sketch, "E22.3.0.52", {"start": v(406.5, -10) * mm, "end": v(405.5, -10) * mm});
            skLineSegment(sketch, "E22.3.0.53", {"start": v(405.5, 45) * mm, "end": v(406.5, 45) * mm});
            skLineSegment(sketch, "E22.3.0.54", {"start": v(405.5, 95) * mm, "end": v(406.5, 95) * mm});
            skLineSegment(sketch, "E22.3.0.55", {"start": v(408.5, 30) * mm, "end": v(407.5, 30) * mm});
            skLineSegment(sketch, "E22.3.0.56", {"start": v(406.5, 40) * mm, "end": v(405.5, 40) * mm});
            skLineSegment(sketch, "E22.3.0.57", {"start": v(405.5, 70) * mm, "end": v(406.5, 70) * mm});
            skLineSegment(sketch, "E22.3.0.58", {"start": v(406.5, 65) * mm, "end": v(405.5, 65) * mm});
            skLineSegment(sketch, "E22.3.0.59", {"start": v(408.5, 130) * mm, "end": v(407.5, 130) * mm});
            skLineSegment(sketch, "E22.4.0.0", {"start": v(401.5, 90) * mm, "end": v(401.5, 70) * mm});
            skLineSegment(sketch, "E22.4.0.1", {"start": v(401.5, 115) * mm, "end": v(401.5, 95) * mm});
            skLineSegment(sketch, "E22.4.0.2", {"start": v(401.5, 65) * mm, "end": v(401.5, 45) * mm});
            skLineSegment(sketch, "E22.4.0.3", {"start": v(402.5, 70) * mm, "end": v(402.5, 90) * mm});
            skLineSegment(sketch, "E22.4.0.4", {"start": v(401.5, 15) * mm, "end": v(401.5, -5) * mm});
            skPoint(sketch, "E22.4.0.5", {"position": v(403.5, 70) * mm});
            skPoint(sketch, "E22.4.0.6", {"position": v(403.5, 120) * mm});
            skPoint(sketch, "E22.4.0.7", {"position": v(403.5, 20) * mm});
            skLineSegment(sketch, "E22.4.0.8", {"start": v(402.5, 45) * mm, "end": v(402.5, 65) * mm});
            skPoint(sketch, "E22.4.0.9", {"position": v(403.5, 95) * mm});
            skLineSegment(sketch, "E22.4.0.10", {"start": v(401.5, 40) * mm, "end": v(401.5, 20) * mm});
            skLineSegment(sketch, "E22.4.0.11", {"start": v(404.5, 110) * mm, "end": v(404.5, 130) * mm});
            skLineSegment(sketch, "E22.4.0.12", {"start": v(403.5, 130) * mm, "end": v(403.5, 110) * mm});
            skLineSegment(sketch, "E22.4.0.13", {"start": v(401.5, -10) * mm, "end": v(401.5, -30) * mm});
            skLineSegment(sketch, "E22.4.0.14", {"start": v(402.5, -5) * mm, "end": v(402.5, 15) * mm});
            skLineSegment(sketch, "E22.4.0.15", {"start": v(402.5, 95) * mm, "end": v(402.5, 115) * mm});
            skPoint(sketch, "E22.4.0.16", {"position": v(403.5, 45) * mm});
            skLineSegment(sketch, "E22.4.0.17", {"start": v(402.5, -30) * mm, "end": v(402.5, -10) * mm});
            skPoint(sketch, "E22.4.0.18", {"position": v(403.5, -5) * mm});
            skLineSegment(sketch, "E22.4.0.19", {"start": v(402.5, 20) * mm, "end": v(402.5, 40) * mm});
            skLineSegment(sketch, "E22.4.0.20", {"start": v(403.5, 105) * mm, "end": v(403.5, 85) * mm});
            skLineSegment(sketch, "E22.4.0.21", {"start": v(404.5, 60) * mm, "end": v(404.5, 80) * mm});
            skLineSegment(sketch, "E22.4.0.22", {"start": v(403.5, 80) * mm, "end": v(403.5, 60) * mm});
            skLineSegment(sketch, "E22.4.0.23", {"start": v(404.5, -15) * mm, "end": v(404.5, 5) * mm});
            skLineSegment(sketch, "E22.4.0.24", {"start": v(403.5, 5) * mm, "end": v(403.5, -15) * mm});
            skLineSegment(sketch, "E22.4.0.25", {"start": v(404.5, 85) * mm, "end": v(404.5, 105) * mm});
            skLineSegment(sketch, "E22.4.0.26", {"start": v(404, 130) * mm, "end": v(404, 110) * mm, "construction": true});
            skLineSegment(sketch, "E22.4.0.27", {"start": v(404, 105) * mm, "end": v(404, 85) * mm, "construction": true});
            skLineSegment(sketch, "E22.4.0.28", {"start": v(404.5, 10) * mm, "end": v(404.5, 30) * mm});
            skLineSegment(sketch, "E22.4.0.29", {"start": v(403.5, 55) * mm, "end": v(403.5, 35) * mm});
            skLineSegment(sketch, "E22.4.0.30", {"start": v(404, 80) * mm, "end": v(404, 60) * mm, "construction": true});
            skLineSegment(sketch, "E22.4.0.31", {"start": v(404, 5) * mm, "end": v(404, -15) * mm, "construction": true});
            skLineSegment(sketch, "E22.4.0.32", {"start": v(404.5, 35) * mm, "end": v(404.5, 55) * mm});
            skLineSegment(sketch, "E22.4.0.33", {"start": v(403.5, 30) * mm, "end": v(403.5, 10) * mm});
            skLineSegment(sketch, "E22.4.0.34", {"start": v(404.5, 80) * mm, "end": v(403.5, 80) * mm});
            skLineSegment(sketch, "E22.4.0.35", {"start": v(404, 30) * mm, "end": v(404, 10) * mm, "construction": true});
            skLineSegment(sketch, "E22.4.0.36", {"start": v(404, 55) * mm, "end": v(404, 35) * mm, "construction": true});
            skLineSegment(sketch, "E22.4.0.37", {"start": v(404.5, 5) * mm, "end": v(403.5, 5) * mm});
            skLineSegment(sketch, "E22.4.0.38", {"start": v(403.5, 85) * mm, "end": v(404.5, 85) * mm});
            skLineSegment(sketch, "E22.4.0.39", {"start": v(403.5, -15) * mm, "end": v(404.5, -15) * mm});
            skLineSegment(sketch, "E22.4.0.40", {"start": v(404.5, 105) * mm, "end": v(403.5, 105) * mm});
            skLineSegment(sketch, "E22.4.0.41", {"start": v(402.5, 115) * mm, "end": v(401.5, 115) * mm});
            skLineSegment(sketch, "E22.4.0.42", {"start": v(403.5, 35) * mm, "end": v(404.5, 35) * mm});
            skLineSegment(sketch, "E22.4.0.43", {"start": v(403.5, 10) * mm, "end": v(404.5, 10) * mm});
            skLineSegment(sketch, "E22.4.0.44", {"start": v(402.5, 15) * mm, "end": v(401.5, 15) * mm});
            skLineSegment(sketch, "E22.4.0.45", {"start": v(404.5, 55) * mm, "end": v(403.5, 55) * mm});
            skLineSegment(sketch, "E22.4.0.46", {"start": v(401.5, 20) * mm, "end": v(402.5, 20) * mm});
            skLineSegment(sketch, "E22.4.0.47", {"start": v(401.5, -5) * mm, "end": v(402.5, -5) * mm});
            skLineSegment(sketch, "E22.4.0.48", {"start": v(402.5, 90) * mm, "end": v(401.5, 90) * mm});
            skLineSegment(sketch, "E22.4.0.49", {"start": v(401.5, -30) * mm, "end": v(402.5, -30) * mm});
            skLineSegment(sketch, "E22.4.0.50", {"start": v(403.5, 60) * mm, "end": v(404.5, 60) * mm});
            skLineSegment(sketch, "E22.4.0.51", {"start": v(403.5, 110) * mm, "end": v(404.5, 110) * mm});
            skLineSegment(sketch, "E22.4.0.52", {"start": v(402.5, -10) * mm, "end": v(401.5, -10) * mm});
            skLineSegment(sketch, "E22.4.0.53", {"start": v(401.5, 45) * mm, "end": v(402.5, 45) * mm});
            skLineSegment(sketch, "E22.4.0.54", {"start": v(401.5, 95) * mm, "end": v(402.5, 95) * mm});
            skLineSegment(sketch, "E22.4.0.55", {"start": v(404.5, 30) * mm, "end": v(403.5, 30) * mm});
            skLineSegment(sketch, "E22.4.0.56", {"start": v(402.5, 40) * mm, "end": v(401.5, 40) * mm});
            skLineSegment(sketch, "E22.4.0.57", {"start": v(401.5, 70) * mm, "end": v(402.5, 70) * mm});
            skLineSegment(sketch, "E22.4.0.58", {"start": v(402.5, 65) * mm, "end": v(401.5, 65) * mm});
            skLineSegment(sketch, "E22.4.0.59", {"start": v(404.5, 130) * mm, "end": v(403.5, 130) * mm});
            skLineSegment(sketch, "E22.5.0.0", {"start": v(397.5, 90) * mm, "end": v(397.5, 70) * mm});
            skLineSegment(sketch, "E22.5.0.1", {"start": v(397.5, 115) * mm, "end": v(397.5, 95) * mm});
            skLineSegment(sketch, "E22.5.0.2", {"start": v(397.5, 65) * mm, "end": v(397.5, 45) * mm});
            skLineSegment(sketch, "E22.5.0.3", {"start": v(398.5, 70) * mm, "end": v(398.5, 90) * mm});
            skLineSegment(sketch, "E22.5.0.4", {"start": v(397.5, 15) * mm, "end": v(397.5, -5) * mm});
            skPoint(sketch, "E22.5.0.5", {"position": v(399.5, 70) * mm});
            skPoint(sketch, "E22.5.0.6", {"position": v(399.5, 120) * mm});
            skPoint(sketch, "E22.5.0.7", {"position": v(399.5, 20) * mm});
            skLineSegment(sketch, "E22.5.0.8", {"start": v(398.5, 45) * mm, "end": v(398.5, 65) * mm});
            skPoint(sketch, "E22.5.0.9", {"position": v(399.5, 95) * mm});
            skLineSegment(sketch, "E22.5.0.10", {"start": v(397.5, 40) * mm, "end": v(397.5, 20) * mm});
            skLineSegment(sketch, "E22.5.0.11", {"start": v(400.5, 110) * mm, "end": v(400.5, 130) * mm});
            skLineSegment(sketch, "E22.5.0.12", {"start": v(399.5, 130) * mm, "end": v(399.5, 110) * mm});
            skLineSegment(sketch, "E22.5.0.13", {"start": v(397.5, -10) * mm, "end": v(397.5, -30) * mm});
            skLineSegment(sketch, "E22.5.0.14", {"start": v(398.5, -5) * mm, "end": v(398.5, 15) * mm});
            skLineSegment(sketch, "E22.5.0.15", {"start": v(398.5, 95) * mm, "end": v(398.5, 115) * mm});
            skPoint(sketch, "E22.5.0.16", {"position": v(399.5, 45) * mm});
            skLineSegment(sketch, "E22.5.0.17", {"start": v(398.5, -30) * mm, "end": v(398.5, -10) * mm});
            skPoint(sketch, "E22.5.0.18", {"position": v(399.5, -5) * mm});
            skLineSegment(sketch, "E22.5.0.19", {"start": v(398.5, 20) * mm, "end": v(398.5, 40) * mm});
            skLineSegment(sketch, "E22.5.0.20", {"start": v(399.5, 105) * mm, "end": v(399.5, 85) * mm});
            skLineSegment(sketch, "E22.5.0.21", {"start": v(400.5, 60) * mm, "end": v(400.5, 80) * mm});
            skLineSegment(sketch, "E22.5.0.22", {"start": v(399.5, 80) * mm, "end": v(399.5, 60) * mm});
            skLineSegment(sketch, "E22.5.0.23", {"start": v(400.5, -15) * mm, "end": v(400.5, 5) * mm});
            skLineSegment(sketch, "E22.5.0.24", {"start": v(399.5, 5) * mm, "end": v(399.5, -15) * mm});
            skLineSegment(sketch, "E22.5.0.25", {"start": v(400.5, 85) * mm, "end": v(400.5, 105) * mm});
            skLineSegment(sketch, "E22.5.0.26", {"start": v(400, 130) * mm, "end": v(400, 110) * mm, "construction": true});
            skLineSegment(sketch, "E22.5.0.27", {"start": v(400, 105) * mm, "end": v(400, 85) * mm, "construction": true});
            skLineSegment(sketch, "E22.5.0.28", {"start": v(400.5, 10) * mm, "end": v(400.5, 30) * mm});
            skLineSegment(sketch, "E22.5.0.29", {"start": v(399.5, 55) * mm, "end": v(399.5, 35) * mm});
            skLineSegment(sketch, "E22.5.0.30", {"start": v(400, 80) * mm, "end": v(400, 60) * mm, "construction": true});
            skLineSegment(sketch, "E22.5.0.31", {"start": v(400, 5) * mm, "end": v(400, -15) * mm, "construction": true});
            skLineSegment(sketch, "E22.5.0.32", {"start": v(400.5, 35) * mm, "end": v(400.5, 55) * mm});
            skLineSegment(sketch, "E22.5.0.33", {"start": v(399.5, 30) * mm, "end": v(399.5, 10) * mm});
            skLineSegment(sketch, "E22.5.0.34", {"start": v(400.5, 80) * mm, "end": v(399.5, 80) * mm});
            skLineSegment(sketch, "E22.5.0.35", {"start": v(400, 30) * mm, "end": v(400, 10) * mm, "construction": true});
            skLineSegment(sketch, "E22.5.0.36", {"start": v(400, 55) * mm, "end": v(400, 35) * mm, "construction": true});
            skLineSegment(sketch, "E22.5.0.37", {"start": v(400.5, 5) * mm, "end": v(399.5, 5) * mm});
            skLineSegment(sketch, "E22.5.0.38", {"start": v(399.5, 85) * mm, "end": v(400.5, 85) * mm});
            skLineSegment(sketch, "E22.5.0.39", {"start": v(399.5, -15) * mm, "end": v(400.5, -15) * mm});
            skLineSegment(sketch, "E22.5.0.40", {"start": v(400.5, 105) * mm, "end": v(399.5, 105) * mm});
            skLineSegment(sketch, "E22.5.0.41", {"start": v(398.5, 115) * mm, "end": v(397.5, 115) * mm});
            skLineSegment(sketch, "E22.5.0.42", {"start": v(399.5, 35) * mm, "end": v(400.5, 35) * mm});
            skLineSegment(sketch, "E22.5.0.43", {"start": v(399.5, 10) * mm, "end": v(400.5, 10) * mm});
            skLineSegment(sketch, "E22.5.0.44", {"start": v(398.5, 15) * mm, "end": v(397.5, 15) * mm});
            skLineSegment(sketch, "E22.5.0.45", {"start": v(400.5, 55) * mm, "end": v(399.5, 55) * mm});
            skLineSegment(sketch, "E22.5.0.46", {"start": v(397.5, 20) * mm, "end": v(398.5, 20) * mm});
            skLineSegment(sketch, "E22.5.0.47", {"start": v(397.5, -5) * mm, "end": v(398.5, -5) * mm});
            skLineSegment(sketch, "E22.5.0.48", {"start": v(398.5, 90) * mm, "end": v(397.5, 90) * mm});
            skLineSegment(sketch, "E22.5.0.49", {"start": v(397.5, -30) * mm, "end": v(398.5, -30) * mm});
            skLineSegment(sketch, "E22.5.0.50", {"start": v(399.5, 60) * mm, "end": v(400.5, 60) * mm});
            skLineSegment(sketch, "E22.5.0.51", {"start": v(399.5, 110) * mm, "end": v(400.5, 110) * mm});
            skLineSegment(sketch, "E22.5.0.52", {"start": v(398.5, -10) * mm, "end": v(397.5, -10) * mm});
            skLineSegment(sketch, "E22.5.0.53", {"start": v(397.5, 45) * mm, "end": v(398.5, 45) * mm});
            skLineSegment(sketch, "E22.5.0.54", {"start": v(397.5, 95) * mm, "end": v(398.5, 95) * mm});
            skLineSegment(sketch, "E22.5.0.55", {"start": v(400.5, 30) * mm, "end": v(399.5, 30) * mm});
            skLineSegment(sketch, "E22.5.0.56", {"start": v(398.5, 40) * mm, "end": v(397.5, 40) * mm});
            skLineSegment(sketch, "E22.5.0.57", {"start": v(397.5, 70) * mm, "end": v(398.5, 70) * mm});
            skLineSegment(sketch, "E22.5.0.58", {"start": v(398.5, 65) * mm, "end": v(397.5, 65) * mm});
            skLineSegment(sketch, "E22.5.0.59", {"start": v(400.5, 130) * mm, "end": v(399.5, 130) * mm});
            skLineSegment(sketch, "E22.6.0.0", {"start": v(393.5, 90) * mm, "end": v(393.5, 70) * mm});
            skLineSegment(sketch, "E22.6.0.1", {"start": v(393.5, 115) * mm, "end": v(393.5, 95) * mm});
            skLineSegment(sketch, "E22.6.0.2", {"start": v(393.5, 65) * mm, "end": v(393.5, 45) * mm});
            skLineSegment(sketch, "E22.6.0.3", {"start": v(394.5, 70) * mm, "end": v(394.5, 90) * mm});
            skLineSegment(sketch, "E22.6.0.4", {"start": v(393.5, 15) * mm, "end": v(393.5, -5) * mm});
            skPoint(sketch, "E22.6.0.5", {"position": v(395.5, 70) * mm});
            skPoint(sketch, "E22.6.0.6", {"position": v(395.5, 120) * mm});
            skPoint(sketch, "E22.6.0.7", {"position": v(395.5, 20) * mm});
            skLineSegment(sketch, "E22.6.0.8", {"start": v(394.5, 45) * mm, "end": v(394.5, 65) * mm});
            skPoint(sketch, "E22.6.0.9", {"position": v(395.5, 95) * mm});
            skLineSegment(sketch, "E22.6.0.10", {"start": v(393.5, 40) * mm, "end": v(393.5, 20) * mm});
            skLineSegment(sketch, "E22.6.0.11", {"start": v(396.5, 110) * mm, "end": v(396.5, 130) * mm});
            skLineSegment(sketch, "E22.6.0.12", {"start": v(395.5, 130) * mm, "end": v(395.5, 110) * mm});
            skLineSegment(sketch, "E22.6.0.13", {"start": v(393.5, -10) * mm, "end": v(393.5, -30) * mm});
            skLineSegment(sketch, "E22.6.0.14", {"start": v(394.5, -5) * mm, "end": v(394.5, 15) * mm});
            skLineSegment(sketch, "E22.6.0.15", {"start": v(394.5, 95) * mm, "end": v(394.5, 115) * mm});
            skPoint(sketch, "E22.6.0.16", {"position": v(395.5, 45) * mm});
            skLineSegment(sketch, "E22.6.0.17", {"start": v(394.5, -30) * mm, "end": v(394.5, -10) * mm});
            skPoint(sketch, "E22.6.0.18", {"position": v(395.5, -5) * mm});
            skLineSegment(sketch, "E22.6.0.19", {"start": v(394.5, 20) * mm, "end": v(394.5, 40) * mm});
            skLineSegment(sketch, "E22.6.0.20", {"start": v(395.5, 105) * mm, "end": v(395.5, 85) * mm});
            skLineSegment(sketch, "E22.6.0.21", {"start": v(396.5, 60) * mm, "end": v(396.5, 80) * mm});
            skLineSegment(sketch, "E22.6.0.22", {"start": v(395.5, 80) * mm, "end": v(395.5, 60) * mm});
            skLineSegment(sketch, "E22.6.0.23", {"start": v(396.5, -15) * mm, "end": v(396.5, 5) * mm});
            skLineSegment(sketch, "E22.6.0.24", {"start": v(395.5, 5) * mm, "end": v(395.5, -15) * mm});
            skLineSegment(sketch, "E22.6.0.25", {"start": v(396.5, 85) * mm, "end": v(396.5, 105) * mm});
            skLineSegment(sketch, "E22.6.0.26", {"start": v(396, 130) * mm, "end": v(396, 110) * mm, "construction": true});
            skLineSegment(sketch, "E22.6.0.27", {"start": v(396, 105) * mm, "end": v(396, 85) * mm, "construction": true});
            skLineSegment(sketch, "E22.6.0.28", {"start": v(396.5, 10) * mm, "end": v(396.5, 30) * mm});
            skLineSegment(sketch, "E22.6.0.29", {"start": v(395.5, 55) * mm, "end": v(395.5, 35) * mm});
            skLineSegment(sketch, "E22.6.0.30", {"start": v(396, 80) * mm, "end": v(396, 60) * mm, "construction": true});
            skLineSegment(sketch, "E22.6.0.31", {"start": v(396, 5) * mm, "end": v(396, -15) * mm, "construction": true});
            skLineSegment(sketch, "E22.6.0.32", {"start": v(396.5, 35) * mm, "end": v(396.5, 55) * mm});
            skLineSegment(sketch, "E22.6.0.33", {"start": v(395.5, 30) * mm, "end": v(395.5, 10) * mm});
            skLineSegment(sketch, "E22.6.0.34", {"start": v(396.5, 80) * mm, "end": v(395.5, 80) * mm});
            skLineSegment(sketch, "E22.6.0.35", {"start": v(396, 30) * mm, "end": v(396, 10) * mm, "construction": true});
            skLineSegment(sketch, "E22.6.0.36", {"start": v(396, 55) * mm, "end": v(396, 35) * mm, "construction": true});
            skLineSegment(sketch, "E22.6.0.37", {"start": v(396.5, 5) * mm, "end": v(395.5, 5) * mm});
            skLineSegment(sketch, "E22.6.0.38", {"start": v(395.5, 85) * mm, "end": v(396.5, 85) * mm});
            skLineSegment(sketch, "E22.6.0.39", {"start": v(395.5, -15) * mm, "end": v(396.5, -15) * mm});
            skLineSegment(sketch, "E22.6.0.40", {"start": v(396.5, 105) * mm, "end": v(395.5, 105) * mm});
            skLineSegment(sketch, "E22.6.0.41", {"start": v(394.5, 115) * mm, "end": v(393.5, 115) * mm});
            skLineSegment(sketch, "E22.6.0.42", {"start": v(395.5, 35) * mm, "end": v(396.5, 35) * mm});
            skLineSegment(sketch, "E22.6.0.43", {"start": v(395.5, 10) * mm, "end": v(396.5, 10) * mm});
            skLineSegment(sketch, "E22.6.0.44", {"start": v(394.5, 15) * mm, "end": v(393.5, 15) * mm});
            skLineSegment(sketch, "E22.6.0.45", {"start": v(396.5, 55) * mm, "end": v(395.5, 55) * mm});
            skLineSegment(sketch, "E22.6.0.46", {"start": v(393.5, 20) * mm, "end": v(394.5, 20) * mm});
            skLineSegment(sketch, "E22.6.0.47", {"start": v(393.5, -5) * mm, "end": v(394.5, -5) * mm});
            skLineSegment(sketch, "E22.6.0.48", {"start": v(394.5, 90) * mm, "end": v(393.5, 90) * mm});
            skLineSegment(sketch, "E22.6.0.49", {"start": v(393.5, -30) * mm, "end": v(394.5, -30) * mm});
            skLineSegment(sketch, "E22.6.0.50", {"start": v(395.5, 60) * mm, "end": v(396.5, 60) * mm});
            skLineSegment(sketch, "E22.6.0.51", {"start": v(395.5, 110) * mm, "end": v(396.5, 110) * mm});
            skLineSegment(sketch, "E22.6.0.52", {"start": v(394.5, -10) * mm, "end": v(393.5, -10) * mm});
            skLineSegment(sketch, "E22.6.0.53", {"start": v(393.5, 45) * mm, "end": v(394.5, 45) * mm});
            skLineSegment(sketch, "E22.6.0.54", {"start": v(393.5, 95) * mm, "end": v(394.5, 95) * mm});
            skLineSegment(sketch, "E22.6.0.55", {"start": v(396.5, 30) * mm, "end": v(395.5, 30) * mm});
            skLineSegment(sketch, "E22.6.0.56", {"start": v(394.5, 40) * mm, "end": v(393.5, 40) * mm});
            skLineSegment(sketch, "E22.6.0.57", {"start": v(393.5, 70) * mm, "end": v(394.5, 70) * mm});
            skLineSegment(sketch, "E22.6.0.58", {"start": v(394.5, 65) * mm, "end": v(393.5, 65) * mm});
            skLineSegment(sketch, "E22.6.0.59", {"start": v(396.5, 130) * mm, "end": v(395.5, 130) * mm});
            skLineSegment(sketch, "E22.7.0.0", {"start": v(389.5, 90) * mm, "end": v(389.5, 70) * mm});
            skLineSegment(sketch, "E22.7.0.1", {"start": v(389.5, 115) * mm, "end": v(389.5, 95) * mm});
            skLineSegment(sketch, "E22.7.0.2", {"start": v(389.5, 65) * mm, "end": v(389.5, 45) * mm});
            skLineSegment(sketch, "E22.7.0.3", {"start": v(390.5, 70) * mm, "end": v(390.5, 90) * mm});
            skLineSegment(sketch, "E22.7.0.4", {"start": v(389.5, 15) * mm, "end": v(389.5, -5) * mm});
            skPoint(sketch, "E22.7.0.5", {"position": v(391.5, 70) * mm});
            skPoint(sketch, "E22.7.0.6", {"position": v(391.5, 120) * mm});
            skPoint(sketch, "E22.7.0.7", {"position": v(391.5, 20) * mm});
            skLineSegment(sketch, "E22.7.0.8", {"start": v(390.5, 45) * mm, "end": v(390.5, 65) * mm});
            skPoint(sketch, "E22.7.0.9", {"position": v(391.5, 95) * mm});
            skLineSegment(sketch, "E22.7.0.10", {"start": v(389.5, 40) * mm, "end": v(389.5, 20) * mm});
            skLineSegment(sketch, "E22.7.0.11", {"start": v(392.5, 110) * mm, "end": v(392.5, 130) * mm});
            skLineSegment(sketch, "E22.7.0.12", {"start": v(391.5, 130) * mm, "end": v(391.5, 110) * mm});
            skLineSegment(sketch, "E22.7.0.13", {"start": v(389.5, -10) * mm, "end": v(389.5, -30) * mm});
            skLineSegment(sketch, "E22.7.0.14", {"start": v(390.5, -5) * mm, "end": v(390.5, 15) * mm});
            skLineSegment(sketch, "E22.7.0.15", {"start": v(390.5, 95) * mm, "end": v(390.5, 115) * mm});
            skPoint(sketch, "E22.7.0.16", {"position": v(391.5, 45) * mm});
            skLineSegment(sketch, "E22.7.0.17", {"start": v(390.5, -30) * mm, "end": v(390.5, -10) * mm});
            skPoint(sketch, "E22.7.0.18", {"position": v(391.5, -5) * mm});
            skLineSegment(sketch, "E22.7.0.19", {"start": v(390.5, 20) * mm, "end": v(390.5, 40) * mm});
            skLineSegment(sketch, "E22.7.0.20", {"start": v(391.5, 105) * mm, "end": v(391.5, 85) * mm});
            skLineSegment(sketch, "E22.7.0.21", {"start": v(392.5, 60) * mm, "end": v(392.5, 80) * mm});
            skLineSegment(sketch, "E22.7.0.22", {"start": v(391.5, 80) * mm, "end": v(391.5, 60) * mm});
            skLineSegment(sketch, "E22.7.0.23", {"start": v(392.5, -15) * mm, "end": v(392.5, 5) * mm});
            skLineSegment(sketch, "E22.7.0.24", {"start": v(391.5, 5) * mm, "end": v(391.5, -15) * mm});
            skLineSegment(sketch, "E22.7.0.25", {"start": v(392.5, 85) * mm, "end": v(392.5, 105) * mm});
            skLineSegment(sketch, "E22.7.0.26", {"start": v(392, 130) * mm, "end": v(392, 110) * mm, "construction": true});
            skLineSegment(sketch, "E22.7.0.27", {"start": v(392, 105) * mm, "end": v(392, 85) * mm, "construction": true});
            skLineSegment(sketch, "E22.7.0.28", {"start": v(392.5, 10) * mm, "end": v(392.5, 30) * mm});
            skLineSegment(sketch, "E22.7.0.29", {"start": v(391.5, 55) * mm, "end": v(391.5, 35) * mm});
            skLineSegment(sketch, "E22.7.0.30", {"start": v(392, 80) * mm, "end": v(392, 60) * mm, "construction": true});
            skLineSegment(sketch, "E22.7.0.31", {"start": v(392, 5) * mm, "end": v(392, -15) * mm, "construction": true});
            skLineSegment(sketch, "E22.7.0.32", {"start": v(392.5, 35) * mm, "end": v(392.5, 55) * mm});
            skLineSegment(sketch, "E22.7.0.33", {"start": v(391.5, 30) * mm, "end": v(391.5, 10) * mm});
            skLineSegment(sketch, "E22.7.0.34", {"start": v(392.5, 80) * mm, "end": v(391.5, 80) * mm});
            skLineSegment(sketch, "E22.7.0.35", {"start": v(392, 30) * mm, "end": v(392, 10) * mm, "construction": true});
            skLineSegment(sketch, "E22.7.0.36", {"start": v(392, 55) * mm, "end": v(392, 35) * mm, "construction": true});
            skLineSegment(sketch, "E22.7.0.37", {"start": v(392.5, 5) * mm, "end": v(391.5, 5) * mm});
            skLineSegment(sketch, "E22.7.0.38", {"start": v(391.5, 85) * mm, "end": v(392.5, 85) * mm});
            skLineSegment(sketch, "E22.7.0.39", {"start": v(391.5, -15) * mm, "end": v(392.5, -15) * mm});
            skLineSegment(sketch, "E22.7.0.40", {"start": v(392.5, 105) * mm, "end": v(391.5, 105) * mm});
            skLineSegment(sketch, "E22.7.0.41", {"start": v(390.5, 115) * mm, "end": v(389.5, 115) * mm});
            skLineSegment(sketch, "E22.7.0.42", {"start": v(391.5, 35) * mm, "end": v(392.5, 35) * mm});
            skLineSegment(sketch, "E22.7.0.43", {"start": v(391.5, 10) * mm, "end": v(392.5, 10) * mm});
            skLineSegment(sketch, "E22.7.0.44", {"start": v(390.5, 15) * mm, "end": v(389.5, 15) * mm});
            skLineSegment(sketch, "E22.7.0.45", {"start": v(392.5, 55) * mm, "end": v(391.5, 55) * mm});
            skLineSegment(sketch, "E22.7.0.46", {"start": v(389.5, 20) * mm, "end": v(390.5, 20) * mm});
            skLineSegment(sketch, "E22.7.0.47", {"start": v(389.5, -5) * mm, "end": v(390.5, -5) * mm});
            skLineSegment(sketch, "E22.7.0.48", {"start": v(390.5, 90) * mm, "end": v(389.5, 90) * mm});
            skLineSegment(sketch, "E22.7.0.49", {"start": v(389.5, -30) * mm, "end": v(390.5, -30) * mm});
            skLineSegment(sketch, "E22.7.0.50", {"start": v(391.5, 60) * mm, "end": v(392.5, 60) * mm});
            skLineSegment(sketch, "E22.7.0.51", {"start": v(391.5, 110) * mm, "end": v(392.5, 110) * mm});
            skLineSegment(sketch, "E22.7.0.52", {"start": v(390.5, -10) * mm, "end": v(389.5, -10) * mm});
            skLineSegment(sketch, "E22.7.0.53", {"start": v(389.5, 45) * mm, "end": v(390.5, 45) * mm});
            skLineSegment(sketch, "E22.7.0.54", {"start": v(389.5, 95) * mm, "end": v(390.5, 95) * mm});
            skLineSegment(sketch, "E22.7.0.55", {"start": v(392.5, 30) * mm, "end": v(391.5, 30) * mm});
            skLineSegment(sketch, "E22.7.0.56", {"start": v(390.5, 40) * mm, "end": v(389.5, 40) * mm});
            skLineSegment(sketch, "E22.7.0.57", {"start": v(389.5, 70) * mm, "end": v(390.5, 70) * mm});
            skLineSegment(sketch, "E22.7.0.58", {"start": v(390.5, 65) * mm, "end": v(389.5, 65) * mm});
            skLineSegment(sketch, "E22.7.0.59", {"start": v(392.5, 130) * mm, "end": v(391.5, 130) * mm});
            skLineSegment(sketch, "E22.direction1", {"start": v(417.5, 70) * mm, "end": v(413.5, 70) * mm, "construction": true});
            skLineSegment(sketch, "E23", {"start": v(423.5, 105) * mm, "end": v(424.5, 105) * mm});
            skLineSegment(sketch, "E24", {"start": v(427.5, 105) * mm, "end": v(428.5, 105) * mm});
            skLineSegment(sketch, "E25", {"start": v(431.5, 105) * mm, "end": v(432.5, 105) * mm});
            skLineSegment(sketch, "E26", {"start": v(435.5, 105) * mm, "end": v(436.5, 105) * mm});
            skLineSegment(sketch, "E27", {"start": v(439.5, 105) * mm, "end": v(440.5, 105) * mm});
            skLineSegment(sketch, "E28", {"start": v(443.5, 105) * mm, "end": v(444.5, 105) * mm});
            skLineSegment(sketch, "E29", {"start": v(447.5, 105) * mm, "end": v(448.5, 105) * mm});
            skLineSegment(sketch, "E30.0.8.0", {"start": v(385.5, 90) * mm, "end": v(385.5, 70) * mm});
            skLineSegment(sketch, "E30.3.8.0", {"start": v(385.5, 115) * mm, "end": v(385.5, 95) * mm});
            skLineSegment(sketch, "E30.6.8.0", {"start": v(385.5, 65) * mm, "end": v(385.5, 45) * mm});
            skLineSegment(sketch, "E30.9.8.0", {"start": v(386.5, 70) * mm, "end": v(386.5, 90) * mm});
            skLineSegment(sketch, "E30.12.8.0", {"start": v(385.5, 15) * mm, "end": v(385.5, -5) * mm});
            skPoint(sketch, "E30.15.8.0", {"position": v(387.5, 70) * mm});
            skPoint(sketch, "E30.16.8.0", {"position": v(387.5, 120) * mm});
            skPoint(sketch, "E30.17.8.0", {"position": v(387.5, 20) * mm});
            skLineSegment(sketch, "E30.18.8.0", {"start": v(386.5, 45) * mm, "end": v(386.5, 65) * mm});
            skPoint(sketch, "E30.21.8.0", {"position": v(387.5, 95) * mm});
            skLineSegment(sketch, "E30.22.8.0", {"start": v(385.5, 40) * mm, "end": v(385.5, 20) * mm});
            skLineSegment(sketch, "E30.25.8.0", {"start": v(388.5, 110) * mm, "end": v(388.5, 130) * mm});
            skLineSegment(sketch, "E30.28.8.0", {"start": v(387.5, 130) * mm, "end": v(387.5, 110) * mm});
            skLineSegment(sketch, "E30.31.8.0", {"start": v(385.5, -10) * mm, "end": v(385.5, -30) * mm});
            skLineSegment(sketch, "E30.34.8.0", {"start": v(386.5, -5) * mm, "end": v(386.5, 15) * mm});
            skLineSegment(sketch, "E30.37.8.0", {"start": v(386.5, 95) * mm, "end": v(386.5, 115) * mm});
            skPoint(sketch, "E30.40.8.0", {"position": v(387.5, 45) * mm});
            skLineSegment(sketch, "E30.41.8.0", {"start": v(386.5, -30) * mm, "end": v(386.5, -10) * mm});
            skPoint(sketch, "E30.44.8.0", {"position": v(387.5, -5) * mm});
            skLineSegment(sketch, "E30.45.8.0", {"start": v(386.5, 20) * mm, "end": v(386.5, 40) * mm});
            skLineSegment(sketch, "E30.48.8.0", {"start": v(387.5, 105) * mm, "end": v(387.5, 85) * mm});
            skLineSegment(sketch, "E30.51.8.0", {"start": v(388.5, 60) * mm, "end": v(388.5, 80) * mm});
            skLineSegment(sketch, "E30.54.8.0", {"start": v(387.5, 80) * mm, "end": v(387.5, 60) * mm});
            skLineSegment(sketch, "E30.57.8.0", {"start": v(388.5, -15) * mm, "end": v(388.5, 5) * mm});
            skLineSegment(sketch, "E30.60.8.0", {"start": v(387.5, 5) * mm, "end": v(387.5, -15) * mm});
            skLineSegment(sketch, "E30.63.8.0", {"start": v(388.5, 85) * mm, "end": v(388.5, 105) * mm});
            skLineSegment(sketch, "E30.66.8.0", {"start": v(388, 130) * mm, "end": v(388, 110) * mm, "construction": true});
            skLineSegment(sketch, "E30.69.8.0", {"start": v(388, 105) * mm, "end": v(388, 85) * mm, "construction": true});
            skLineSegment(sketch, "E30.72.8.0", {"start": v(388.5, 10) * mm, "end": v(388.5, 30) * mm});
            skLineSegment(sketch, "E30.75.8.0", {"start": v(387.5, 55) * mm, "end": v(387.5, 35) * mm});
            skLineSegment(sketch, "E30.78.8.0", {"start": v(388, 80) * mm, "end": v(388, 60) * mm, "construction": true});
            skLineSegment(sketch, "E30.81.8.0", {"start": v(388, 5) * mm, "end": v(388, -15) * mm, "construction": true});
            skLineSegment(sketch, "E30.84.8.0", {"start": v(388.5, 35) * mm, "end": v(388.5, 55) * mm});
            skLineSegment(sketch, "E30.87.8.0", {"start": v(387.5, 30) * mm, "end": v(387.5, 10) * mm});
            skLineSegment(sketch, "E30.90.8.0", {"start": v(388.5, 80) * mm, "end": v(387.5, 80) * mm});
            skLineSegment(sketch, "E30.93.8.0", {"start": v(388, 30) * mm, "end": v(388, 10) * mm, "construction": true});
            skLineSegment(sketch, "E30.96.8.0", {"start": v(388, 55) * mm, "end": v(388, 35) * mm, "construction": true});
            skLineSegment(sketch, "E30.99.8.0", {"start": v(388.5, 5) * mm, "end": v(387.5, 5) * mm});
            skLineSegment(sketch, "E30.102.8.0", {"start": v(387.5, 85) * mm, "end": v(388.5, 85) * mm});
            skLineSegment(sketch, "E30.105.8.0", {"start": v(387.5, -15) * mm, "end": v(388.5, -15) * mm});
            skLineSegment(sketch, "E30.108.8.0", {"start": v(388.5, 105) * mm, "end": v(387.5, 105) * mm});
            skLineSegment(sketch, "E30.111.8.0", {"start": v(386.5, 115) * mm, "end": v(385.5, 115) * mm});
            skLineSegment(sketch, "E30.114.8.0", {"start": v(387.5, 35) * mm, "end": v(388.5, 35) * mm});
            skLineSegment(sketch, "E30.117.8.0", {"start": v(387.5, 10) * mm, "end": v(388.5, 10) * mm});
            skLineSegment(sketch, "E30.120.8.0", {"start": v(386.5, 15) * mm, "end": v(385.5, 15) * mm});
            skLineSegment(sketch, "E30.123.8.0", {"start": v(388.5, 55) * mm, "end": v(387.5, 55) * mm});
            skLineSegment(sketch, "E30.126.8.0", {"start": v(385.5, 20) * mm, "end": v(386.5, 20) * mm});
            skLineSegment(sketch, "E30.129.8.0", {"start": v(385.5, -5) * mm, "end": v(386.5, -5) * mm});
            skLineSegment(sketch, "E30.132.8.0", {"start": v(386.5, 90) * mm, "end": v(385.5, 90) * mm});
            skLineSegment(sketch, "E30.135.8.0", {"start": v(385.5, -30) * mm, "end": v(386.5, -30) * mm});
            skLineSegment(sketch, "E30.138.8.0", {"start": v(387.5, 60) * mm, "end": v(388.5, 60) * mm});
            skLineSegment(sketch, "E30.141.8.0", {"start": v(387.5, 110) * mm, "end": v(388.5, 110) * mm});
            skLineSegment(sketch, "E30.144.8.0", {"start": v(386.5, -10) * mm, "end": v(385.5, -10) * mm});
            skLineSegment(sketch, "E30.147.8.0", {"start": v(385.5, 45) * mm, "end": v(386.5, 45) * mm});
            skLineSegment(sketch, "E30.150.8.0", {"start": v(385.5, 95) * mm, "end": v(386.5, 95) * mm});
            skLineSegment(sketch, "E30.153.8.0", {"start": v(388.5, 30) * mm, "end": v(387.5, 30) * mm});
            skLineSegment(sketch, "E30.156.8.0", {"start": v(386.5, 40) * mm, "end": v(385.5, 40) * mm});
            skLineSegment(sketch, "E30.159.8.0", {"start": v(385.5, 70) * mm, "end": v(386.5, 70) * mm});
            skLineSegment(sketch, "E30.162.8.0", {"start": v(386.5, 65) * mm, "end": v(385.5, 65) * mm});
            skLineSegment(sketch, "E30.165.8.0", {"start": v(388.5, 130) * mm, "end": v(387.5, 130) * mm});
            skLineSegment(sketch, "E30.0.9.0", {"start": v(381.5, 90) * mm, "end": v(381.5, 70) * mm});
            skLineSegment(sketch, "E30.3.9.0", {"start": v(381.5, 115) * mm, "end": v(381.5, 95) * mm});
            skLineSegment(sketch, "E30.6.9.0", {"start": v(381.5, 65) * mm, "end": v(381.5, 45) * mm});
            skLineSegment(sketch, "E30.9.9.0", {"start": v(382.5, 70) * mm, "end": v(382.5, 90) * mm});
            skLineSegment(sketch, "E30.12.9.0", {"start": v(381.5, 15) * mm, "end": v(381.5, -5) * mm});
            skPoint(sketch, "E30.15.9.0", {"position": v(383.5, 70) * mm});
            skPoint(sketch, "E30.16.9.0", {"position": v(383.5, 120) * mm});
            skPoint(sketch, "E30.17.9.0", {"position": v(383.5, 20) * mm});
            skLineSegment(sketch, "E30.18.9.0", {"start": v(382.5, 45) * mm, "end": v(382.5, 65) * mm});
            skPoint(sketch, "E30.21.9.0", {"position": v(383.5, 95) * mm});
            skLineSegment(sketch, "E30.22.9.0", {"start": v(381.5, 40) * mm, "end": v(381.5, 20) * mm});
            skLineSegment(sketch, "E30.25.9.0", {"start": v(384.5, 110) * mm, "end": v(384.5, 130) * mm});
            skLineSegment(sketch, "E30.28.9.0", {"start": v(383.5, 130) * mm, "end": v(383.5, 110) * mm});
            skLineSegment(sketch, "E30.31.9.0", {"start": v(381.5, -10) * mm, "end": v(381.5, -30) * mm});
            skLineSegment(sketch, "E30.34.9.0", {"start": v(382.5, -5) * mm, "end": v(382.5, 15) * mm});
            skLineSegment(sketch, "E30.37.9.0", {"start": v(382.5, 95) * mm, "end": v(382.5, 115) * mm});
            skPoint(sketch, "E30.40.9.0", {"position": v(383.5, 45) * mm});
            skLineSegment(sketch, "E30.41.9.0", {"start": v(382.5, -30) * mm, "end": v(382.5, -10) * mm});
            skPoint(sketch, "E30.44.9.0", {"position": v(383.5, -5) * mm});
            skLineSegment(sketch, "E30.45.9.0", {"start": v(382.5, 20) * mm, "end": v(382.5, 40) * mm});
            skLineSegment(sketch, "E30.48.9.0", {"start": v(383.5, 105) * mm, "end": v(383.5, 85) * mm});
            skLineSegment(sketch, "E30.51.9.0", {"start": v(384.5, 60) * mm, "end": v(384.5, 80) * mm});
            skLineSegment(sketch, "E30.54.9.0", {"start": v(383.5, 80) * mm, "end": v(383.5, 60) * mm});
            skLineSegment(sketch, "E30.57.9.0", {"start": v(384.5, -15) * mm, "end": v(384.5, 5) * mm});
            skLineSegment(sketch, "E30.60.9.0", {"start": v(383.5, 5) * mm, "end": v(383.5, -15) * mm});
            skLineSegment(sketch, "E30.63.9.0", {"start": v(384.5, 85) * mm, "end": v(384.5, 105) * mm});
            skLineSegment(sketch, "E30.66.9.0", {"start": v(384, 130) * mm, "end": v(384, 110) * mm, "construction": true});
            skLineSegment(sketch, "E30.69.9.0", {"start": v(384, 105) * mm, "end": v(384, 85) * mm, "construction": true});
            skLineSegment(sketch, "E30.72.9.0", {"start": v(384.5, 10) * mm, "end": v(384.5, 30) * mm});
            skLineSegment(sketch, "E30.75.9.0", {"start": v(383.5, 55) * mm, "end": v(383.5, 35) * mm});
            skLineSegment(sketch, "E30.78.9.0", {"start": v(384, 80) * mm, "end": v(384, 60) * mm, "construction": true});
            skLineSegment(sketch, "E30.81.9.0", {"start": v(384, 5) * mm, "end": v(384, -15) * mm, "construction": true});
            skLineSegment(sketch, "E30.84.9.0", {"start": v(384.5, 35) * mm, "end": v(384.5, 55) * mm});
            skLineSegment(sketch, "E30.87.9.0", {"start": v(383.5, 30) * mm, "end": v(383.5, 10) * mm});
            skLineSegment(sketch, "E30.90.9.0", {"start": v(384.5, 80) * mm, "end": v(383.5, 80) * mm});
            skLineSegment(sketch, "E30.93.9.0", {"start": v(384, 30) * mm, "end": v(384, 10) * mm, "construction": true});
            skLineSegment(sketch, "E30.96.9.0", {"start": v(384, 55) * mm, "end": v(384, 35) * mm, "construction": true});
            skLineSegment(sketch, "E30.99.9.0", {"start": v(384.5, 5) * mm, "end": v(383.5, 5) * mm});
            skLineSegment(sketch, "E30.102.9.0", {"start": v(383.5, 85) * mm, "end": v(384.5, 85) * mm});
            skLineSegment(sketch, "E30.105.9.0", {"start": v(383.5, -15) * mm, "end": v(384.5, -15) * mm});
            skLineSegment(sketch, "E30.108.9.0", {"start": v(384.5, 105) * mm, "end": v(383.5, 105) * mm});
            skLineSegment(sketch, "E30.111.9.0", {"start": v(382.5, 115) * mm, "end": v(381.5, 115) * mm});
            skLineSegment(sketch, "E30.114.9.0", {"start": v(383.5, 35) * mm, "end": v(384.5, 35) * mm});
            skLineSegment(sketch, "E30.117.9.0", {"start": v(383.5, 10) * mm, "end": v(384.5, 10) * mm});
            skLineSegment(sketch, "E30.120.9.0", {"start": v(382.5, 15) * mm, "end": v(381.5, 15) * mm});
            skLineSegment(sketch, "E30.123.9.0", {"start": v(384.5, 55) * mm, "end": v(383.5, 55) * mm});
            skLineSegment(sketch, "E30.126.9.0", {"start": v(381.5, 20) * mm, "end": v(382.5, 20) * mm});
            skLineSegment(sketch, "E30.129.9.0", {"start": v(381.5, -5) * mm, "end": v(382.5, -5) * mm});
            skLineSegment(sketch, "E30.132.9.0", {"start": v(382.5, 90) * mm, "end": v(381.5, 90) * mm});
            skLineSegment(sketch, "E30.135.9.0", {"start": v(381.5, -30) * mm, "end": v(382.5, -30) * mm});
            skLineSegment(sketch, "E30.138.9.0", {"start": v(383.5, 60) * mm, "end": v(384.5, 60) * mm});
            skLineSegment(sketch, "E30.141.9.0", {"start": v(383.5, 110) * mm, "end": v(384.5, 110) * mm});
            skLineSegment(sketch, "E30.144.9.0", {"start": v(382.5, -10) * mm, "end": v(381.5, -10) * mm});
            skLineSegment(sketch, "E30.147.9.0", {"start": v(381.5, 45) * mm, "end": v(382.5, 45) * mm});
            skLineSegment(sketch, "E30.150.9.0", {"start": v(381.5, 95) * mm, "end": v(382.5, 95) * mm});
            skLineSegment(sketch, "E30.153.9.0", {"start": v(384.5, 30) * mm, "end": v(383.5, 30) * mm});
            skLineSegment(sketch, "E30.156.9.0", {"start": v(382.5, 40) * mm, "end": v(381.5, 40) * mm});
            skLineSegment(sketch, "E30.159.9.0", {"start": v(381.5, 70) * mm, "end": v(382.5, 70) * mm});
            skLineSegment(sketch, "E30.162.9.0", {"start": v(382.5, 65) * mm, "end": v(381.5, 65) * mm});
            skLineSegment(sketch, "E30.165.9.0", {"start": v(384.5, 130) * mm, "end": v(383.5, 130) * mm});
            skLineSegment(sketch, "E31.0.8.0", {"start": v(454.5, -10) * mm, "end": v(454.5, -30) * mm});
            skPoint(sketch, "E31.3.8.0", {"position": v(451.5, 95) * mm});
            skLineSegment(sketch, "E31.4.8.0", {"start": v(453.5, 70) * mm, "end": v(453.5, 90) * mm});
            skLineSegment(sketch, "E31.7.8.0", {"start": v(453.5, 45) * mm, "end": v(453.5, 65) * mm});
            skLineSegment(sketch, "E31.10.8.0", {"start": v(454.5, 65) * mm, "end": v(454.5, 45) * mm});
            skPoint(sketch, "E31.13.8.0", {"position": v(451.5, 70) * mm});
            skLineSegment(sketch, "E31.14.8.0", {"start": v(453.5, -5) * mm, "end": v(453.5, 15) * mm});
            skPoint(sketch, "E31.17.8.0", {"position": v(451.5, 20) * mm});
            skLineSegment(sketch, "E31.18.8.0", {"start": v(454.5, 40) * mm, "end": v(454.5, 20) * mm});
            skLineSegment(sketch, "E31.21.8.0", {"start": v(453.5, -30) * mm, "end": v(453.5, -10) * mm});
            skPoint(sketch, "E31.24.8.0", {"position": v(451.5, 45) * mm});
            skLineSegment(sketch, "E31.25.8.0", {"start": v(453.5, 20) * mm, "end": v(453.5, 40) * mm});
            skLineSegment(sketch, "E31.28.8.0", {"start": v(454.5, 90) * mm, "end": v(454.5, 70) * mm});
            skLineSegment(sketch, "E31.31.8.0", {"start": v(454.5, 15) * mm, "end": v(454.5, -5) * mm});
            skPoint(sketch, "E31.34.8.0", {"position": v(451.5, -5) * mm});
            skLineSegment(sketch, "E31.35.8.0", {"start": v(452.5, 85) * mm, "end": v(452.5, 105) * mm});
            skLineSegment(sketch, "E31.38.8.0", {"start": v(454.5, 95) * mm, "end": v(454.5, 70) * mm, "construction": true});
            skLineSegment(sketch, "E31.41.8.0", {"start": v(452.5, 35) * mm, "end": v(452.5, 55) * mm});
            skLineSegment(sketch, "E31.44.8.0", {"start": v(452.5, 60) * mm, "end": v(452.5, 80) * mm});
            skLineSegment(sketch, "E31.47.8.0", {"start": v(452.5, -15) * mm, "end": v(452.5, 5) * mm});
            skLineSegment(sketch, "E31.50.8.0", {"start": v(451.5, 80) * mm, "end": v(451.5, 60) * mm});
            skLineSegment(sketch, "E31.53.8.0", {"start": v(453.5, 15) * mm, "end": v(454.5, 15) * mm});
            skLineSegment(sketch, "E31.56.8.0", {"start": v(451.5, 105) * mm, "end": v(451.5, 85) * mm});
            skLineSegment(sketch, "E31.59.8.0", {"start": v(451.5, 55) * mm, "end": v(451.5, 35) * mm});
            skLineSegment(sketch, "E31.62.8.0", {"start": v(453.5, -10) * mm, "end": v(454.5, -10) * mm});
            skLineSegment(sketch, "E31.65.8.0", {"start": v(452, 55) * mm, "end": v(452, 35) * mm, "construction": true});
            skLineSegment(sketch, "E31.68.8.0", {"start": v(454.5, -5) * mm, "end": v(453.5, -5) * mm});
            skLineSegment(sketch, "E31.71.8.0", {"start": v(451.5, 5) * mm, "end": v(451.5, -15) * mm});
            skLineSegment(sketch, "E31.74.8.0", {"start": v(452, 105) * mm, "end": v(452, 85) * mm, "construction": true});
            skLineSegment(sketch, "E31.77.8.0", {"start": v(452.5, 10) * mm, "end": v(452.5, 30) * mm});
            skLineSegment(sketch, "E31.80.8.0", {"start": v(453.5, 40) * mm, "end": v(454.5, 40) * mm});
            skLineSegment(sketch, "E31.83.8.0", {"start": v(452, 80) * mm, "end": v(452, 60) * mm, "construction": true});
            skLineSegment(sketch, "E31.86.8.0", {"start": v(452, 5) * mm, "end": v(452, -15) * mm, "construction": true});
            skLineSegment(sketch, "E31.89.8.0", {"start": v(454.5, -30) * mm, "end": v(453.5, -30) * mm});
            skLineSegment(sketch, "E31.92.8.0", {"start": v(451.5, 35) * mm, "end": v(452.5, 35) * mm});
            skLineSegment(sketch, "E31.95.8.0", {"start": v(454.5, 20) * mm, "end": v(453.5, 20) * mm});
            skLineSegment(sketch, "E31.98.8.0", {"start": v(454.5, 70) * mm, "end": v(453.5, 70) * mm});
            skLineSegment(sketch, "E31.101.8.0", {"start": v(451.5, -15) * mm, "end": v(452.5, -15) * mm});
            skLineSegment(sketch, "E31.104.8.0", {"start": v(452.5, 30) * mm, "end": v(451.5, 30) * mm});
            skLineSegment(sketch, "E31.107.8.0", {"start": v(452.5, 5) * mm, "end": v(451.5, 5) * mm});
            skLineSegment(sketch, "E31.110.8.0", {"start": v(451.5, 60) * mm, "end": v(452.5, 60) * mm});
            skLineSegment(sketch, "E31.113.8.0", {"start": v(452, 30) * mm, "end": v(452, 10) * mm, "construction": true});
            skLineSegment(sketch, "E31.116.8.0", {"start": v(453.5, 90) * mm, "end": v(454.5, 90) * mm});
            skLineSegment(sketch, "E31.119.8.0", {"start": v(452.5, 80) * mm, "end": v(451.5, 80) * mm});
            skLineSegment(sketch, "E31.122.8.0", {"start": v(451.5, 30) * mm, "end": v(451.5, 10) * mm});
            skLineSegment(sketch, "E31.125.8.0", {"start": v(452.5, 55) * mm, "end": v(451.5, 55) * mm});
            skLineSegment(sketch, "E31.128.8.0", {"start": v(451.5, 85) * mm, "end": v(452.5, 85) * mm});
            skLineSegment(sketch, "E31.131.8.0", {"start": v(451.5, 10) * mm, "end": v(452.5, 10) * mm});
            skLineSegment(sketch, "E31.134.8.0", {"start": v(453.5, 65) * mm, "end": v(454.5, 65) * mm});
            skLineSegment(sketch, "E31.137.8.0", {"start": v(454.5, 45) * mm, "end": v(453.5, 45) * mm});
            skLineSegment(sketch, "E31.140.8.0", {"start": v(453.5, 95) * mm, "end": v(453.5, 115) * mm});
            skLineSegment(sketch, "E31.143.8.0", {"start": v(454.5, 95) * mm, "end": v(453.5, 95) * mm});
            skLineSegment(sketch, "E31.146.8.0", {"start": v(454.5, 115) * mm, "end": v(454.5, 95) * mm});
            skLineSegment(sketch, "E31.149.8.0", {"start": v(453.5, 115) * mm, "end": v(454.5, 115) * mm});
            skLineSegment(sketch, "E31.152.8.0", {"start": v(452.5, 110) * mm, "end": v(452.5, 130) * mm});
            skLineSegment(sketch, "E31.155.8.0", {"start": v(451.5, 130) * mm, "end": v(451.5, 110) * mm});
            skLineSegment(sketch, "E31.158.8.0", {"start": v(451.5, 110) * mm, "end": v(452.5, 110) * mm});
            skLineSegment(sketch, "E31.161.8.0", {"start": v(452.5, 130) * mm, "end": v(451.5, 130) * mm});
            skLineSegment(sketch, "E31.0.9.0", {"start": v(458.5, -10) * mm, "end": v(458.5, -30) * mm});
            skPoint(sketch, "E31.3.9.0", {"position": v(455.5, 95) * mm});
            skLineSegment(sketch, "E31.4.9.0", {"start": v(457.5, 70) * mm, "end": v(457.5, 90) * mm});
            skLineSegment(sketch, "E31.7.9.0", {"start": v(457.5, 45) * mm, "end": v(457.5, 65) * mm});
            skLineSegment(sketch, "E31.10.9.0", {"start": v(458.5, 65) * mm, "end": v(458.5, 45) * mm});
            skPoint(sketch, "E31.13.9.0", {"position": v(455.5, 70) * mm});
            skLineSegment(sketch, "E31.14.9.0", {"start": v(457.5, -5) * mm, "end": v(457.5, 15) * mm});
            skPoint(sketch, "E31.17.9.0", {"position": v(455.5, 20) * mm});
            skLineSegment(sketch, "E31.18.9.0", {"start": v(458.5, 40) * mm, "end": v(458.5, 20) * mm});
            skLineSegment(sketch, "E31.21.9.0", {"start": v(457.5, -30) * mm, "end": v(457.5, -10) * mm});
            skPoint(sketch, "E31.24.9.0", {"position": v(455.5, 45) * mm});
            skLineSegment(sketch, "E31.25.9.0", {"start": v(457.5, 20) * mm, "end": v(457.5, 40) * mm});
            skLineSegment(sketch, "E31.28.9.0", {"start": v(458.5, 90) * mm, "end": v(458.5, 70) * mm});
            skLineSegment(sketch, "E31.31.9.0", {"start": v(458.5, 15) * mm, "end": v(458.5, -5) * mm});
            skPoint(sketch, "E31.34.9.0", {"position": v(455.5, -5) * mm});
            skLineSegment(sketch, "E31.35.9.0", {"start": v(456.5, 85) * mm, "end": v(456.5, 105) * mm});
            skLineSegment(sketch, "E31.38.9.0", {"start": v(458.5, 95) * mm, "end": v(458.5, 70) * mm, "construction": true});
            skLineSegment(sketch, "E31.41.9.0", {"start": v(456.5, 35) * mm, "end": v(456.5, 55) * mm});
            skLineSegment(sketch, "E31.44.9.0", {"start": v(456.5, 60) * mm, "end": v(456.5, 80) * mm});
            skLineSegment(sketch, "E31.47.9.0", {"start": v(456.5, -15) * mm, "end": v(456.5, 5) * mm});
            skLineSegment(sketch, "E31.50.9.0", {"start": v(455.5, 80) * mm, "end": v(455.5, 60) * mm});
            skLineSegment(sketch, "E31.53.9.0", {"start": v(457.5, 15) * mm, "end": v(458.5, 15) * mm});
            skLineSegment(sketch, "E31.56.9.0", {"start": v(455.5, 105) * mm, "end": v(455.5, 85) * mm});
            skLineSegment(sketch, "E31.59.9.0", {"start": v(455.5, 55) * mm, "end": v(455.5, 35) * mm});
            skLineSegment(sketch, "E31.62.9.0", {"start": v(457.5, -10) * mm, "end": v(458.5, -10) * mm});
            skLineSegment(sketch, "E31.65.9.0", {"start": v(456, 55) * mm, "end": v(456, 35) * mm, "construction": true});
            skLineSegment(sketch, "E31.68.9.0", {"start": v(458.5, -5) * mm, "end": v(457.5, -5) * mm});
            skLineSegment(sketch, "E31.71.9.0", {"start": v(455.5, 5) * mm, "end": v(455.5, -15) * mm});
            skLineSegment(sketch, "E31.74.9.0", {"start": v(456, 105) * mm, "end": v(456, 85) * mm, "construction": true});
            skLineSegment(sketch, "E31.77.9.0", {"start": v(456.5, 10) * mm, "end": v(456.5, 30) * mm});
            skLineSegment(sketch, "E31.80.9.0", {"start": v(457.5, 40) * mm, "end": v(458.5, 40) * mm});
            skLineSegment(sketch, "E31.83.9.0", {"start": v(456, 80) * mm, "end": v(456, 60) * mm, "construction": true});
            skLineSegment(sketch, "E31.86.9.0", {"start": v(456, 5) * mm, "end": v(456, -15) * mm, "construction": true});
            skLineSegment(sketch, "E31.89.9.0", {"start": v(458.5, -30) * mm, "end": v(457.5, -30) * mm});
            skLineSegment(sketch, "E31.92.9.0", {"start": v(455.5, 35) * mm, "end": v(456.5, 35) * mm});
            skLineSegment(sketch, "E31.95.9.0", {"start": v(458.5, 20) * mm, "end": v(457.5, 20) * mm});
            skLineSegment(sketch, "E31.98.9.0", {"start": v(458.5, 70) * mm, "end": v(457.5, 70) * mm});
            skLineSegment(sketch, "E31.101.9.0", {"start": v(455.5, -15) * mm, "end": v(456.5, -15) * mm});
            skLineSegment(sketch, "E31.104.9.0", {"start": v(456.5, 30) * mm, "end": v(455.5, 30) * mm});
            skLineSegment(sketch, "E31.107.9.0", {"start": v(456.5, 5) * mm, "end": v(455.5, 5) * mm});
            skLineSegment(sketch, "E31.110.9.0", {"start": v(455.5, 60) * mm, "end": v(456.5, 60) * mm});
            skLineSegment(sketch, "E31.113.9.0", {"start": v(456, 30) * mm, "end": v(456, 10) * mm, "construction": true});
            skLineSegment(sketch, "E31.116.9.0", {"start": v(457.5, 90) * mm, "end": v(458.5, 90) * mm});
            skLineSegment(sketch, "E31.119.9.0", {"start": v(456.5, 80) * mm, "end": v(455.5, 80) * mm});
            skLineSegment(sketch, "E31.122.9.0", {"start": v(455.5, 30) * mm, "end": v(455.5, 10) * mm});
            skLineSegment(sketch, "E31.125.9.0", {"start": v(456.5, 55) * mm, "end": v(455.5, 55) * mm});
            skLineSegment(sketch, "E31.128.9.0", {"start": v(455.5, 85) * mm, "end": v(456.5, 85) * mm});
            skLineSegment(sketch, "E31.131.9.0", {"start": v(455.5, 10) * mm, "end": v(456.5, 10) * mm});
            skLineSegment(sketch, "E31.134.9.0", {"start": v(457.5, 65) * mm, "end": v(458.5, 65) * mm});
            skLineSegment(sketch, "E31.137.9.0", {"start": v(458.5, 45) * mm, "end": v(457.5, 45) * mm});
            skLineSegment(sketch, "E31.140.9.0", {"start": v(457.5, 95) * mm, "end": v(457.5, 115) * mm});
            skLineSegment(sketch, "E31.143.9.0", {"start": v(458.5, 95) * mm, "end": v(457.5, 95) * mm});
            skLineSegment(sketch, "E31.146.9.0", {"start": v(458.5, 115) * mm, "end": v(458.5, 95) * mm});
            skLineSegment(sketch, "E31.149.9.0", {"start": v(457.5, 115) * mm, "end": v(458.5, 115) * mm});
            skLineSegment(sketch, "E31.152.9.0", {"start": v(456.5, 110) * mm, "end": v(456.5, 130) * mm});
            skLineSegment(sketch, "E31.155.9.0", {"start": v(455.5, 130) * mm, "end": v(455.5, 110) * mm});
            skLineSegment(sketch, "E31.158.9.0", {"start": v(455.5, 110) * mm, "end": v(456.5, 110) * mm});
            skLineSegment(sketch, "E31.161.9.0", {"start": v(456.5, 130) * mm, "end": v(455.5, 130) * mm});
            skLineSegment(sketch, "E32.0.10.0", {"start": v(462.5, -10) * mm, "end": v(462.5, -30) * mm});
            skPoint(sketch, "E32.3.10.0", {"position": v(459.5, 95) * mm});
            skLineSegment(sketch, "E32.4.10.0", {"start": v(461.5, 70) * mm, "end": v(461.5, 90) * mm});
            skLineSegment(sketch, "E32.7.10.0", {"start": v(461.5, 45) * mm, "end": v(461.5, 65) * mm});
            skLineSegment(sketch, "E32.10.10.0", {"start": v(462.5, 65) * mm, "end": v(462.5, 45) * mm});
            skPoint(sketch, "E32.13.10.0", {"position": v(459.5, 70) * mm});
            skLineSegment(sketch, "E32.14.10.0", {"start": v(461.5, -5) * mm, "end": v(461.5, 15) * mm});
            skPoint(sketch, "E32.17.10.0", {"position": v(459.5, 20) * mm});
            skLineSegment(sketch, "E32.18.10.0", {"start": v(462.5, 40) * mm, "end": v(462.5, 20) * mm});
            skLineSegment(sketch, "E32.21.10.0", {"start": v(461.5, -30) * mm, "end": v(461.5, -10) * mm});
            skPoint(sketch, "E32.24.10.0", {"position": v(459.5, 45) * mm});
            skLineSegment(sketch, "E32.25.10.0", {"start": v(461.5, 20) * mm, "end": v(461.5, 40) * mm});
            skLineSegment(sketch, "E32.28.10.0", {"start": v(462.5, 90) * mm, "end": v(462.5, 70) * mm});
            skLineSegment(sketch, "E32.31.10.0", {"start": v(462.5, 15) * mm, "end": v(462.5, -5) * mm});
            skPoint(sketch, "E32.34.10.0", {"position": v(459.5, -5) * mm});
            skLineSegment(sketch, "E32.35.10.0", {"start": v(460.5, 85) * mm, "end": v(460.5, 105) * mm});
            skLineSegment(sketch, "E32.38.10.0", {"start": v(462.5, 95) * mm, "end": v(462.5, 70) * mm, "construction": true});
            skLineSegment(sketch, "E32.41.10.0", {"start": v(460.5, 35) * mm, "end": v(460.5, 55) * mm});
            skLineSegment(sketch, "E32.44.10.0", {"start": v(460.5, 60) * mm, "end": v(460.5, 80) * mm});
            skLineSegment(sketch, "E32.47.10.0", {"start": v(460.5, -15) * mm, "end": v(460.5, 5) * mm});
            skLineSegment(sketch, "E32.50.10.0", {"start": v(459.5, 80) * mm, "end": v(459.5, 60) * mm});
            skLineSegment(sketch, "E32.53.10.0", {"start": v(461.5, 15) * mm, "end": v(462.5, 15) * mm});
            skLineSegment(sketch, "E32.56.10.0", {"start": v(459.5, 105) * mm, "end": v(459.5, 85) * mm});
            skLineSegment(sketch, "E32.59.10.0", {"start": v(459.5, 55) * mm, "end": v(459.5, 35) * mm});
            skLineSegment(sketch, "E32.62.10.0", {"start": v(461.5, -10) * mm, "end": v(462.5, -10) * mm});
            skLineSegment(sketch, "E32.65.10.0", {"start": v(460, 55) * mm, "end": v(460, 35) * mm, "construction": true});
            skLineSegment(sketch, "E32.68.10.0", {"start": v(462.5, -5) * mm, "end": v(461.5, -5) * mm});
            skLineSegment(sketch, "E32.71.10.0", {"start": v(459.5, 5) * mm, "end": v(459.5, -15) * mm});
            skLineSegment(sketch, "E32.74.10.0", {"start": v(460, 105) * mm, "end": v(460, 85) * mm, "construction": true});
            skLineSegment(sketch, "E32.77.10.0", {"start": v(460.5, 10) * mm, "end": v(460.5, 30) * mm});
            skLineSegment(sketch, "E32.80.10.0", {"start": v(461.5, 40) * mm, "end": v(462.5, 40) * mm});
            skLineSegment(sketch, "E32.83.10.0", {"start": v(460, 80) * mm, "end": v(460, 60) * mm, "construction": true});
            skLineSegment(sketch, "E32.86.10.0", {"start": v(460, 5) * mm, "end": v(460, -15) * mm, "construction": true});
            skLineSegment(sketch, "E32.89.10.0", {"start": v(462.5, -30) * mm, "end": v(461.5, -30) * mm});
            skLineSegment(sketch, "E32.92.10.0", {"start": v(459.5, 35) * mm, "end": v(460.5, 35) * mm});
            skLineSegment(sketch, "E32.95.10.0", {"start": v(462.5, 20) * mm, "end": v(461.5, 20) * mm});
            skLineSegment(sketch, "E32.98.10.0", {"start": v(462.5, 70) * mm, "end": v(461.5, 70) * mm});
            skLineSegment(sketch, "E32.101.10.0", {"start": v(459.5, -15) * mm, "end": v(460.5, -15) * mm});
            skLineSegment(sketch, "E32.104.10.0", {"start": v(460.5, 30) * mm, "end": v(459.5, 30) * mm});
            skLineSegment(sketch, "E32.107.10.0", {"start": v(460.5, 5) * mm, "end": v(459.5, 5) * mm});
            skLineSegment(sketch, "E32.110.10.0", {"start": v(459.5, 60) * mm, "end": v(460.5, 60) * mm});
            skLineSegment(sketch, "E32.113.10.0", {"start": v(460, 30) * mm, "end": v(460, 10) * mm, "construction": true});
            skLineSegment(sketch, "E32.116.10.0", {"start": v(461.5, 90) * mm, "end": v(462.5, 90) * mm});
            skLineSegment(sketch, "E32.119.10.0", {"start": v(460.5, 80) * mm, "end": v(459.5, 80) * mm});
            skLineSegment(sketch, "E32.122.10.0", {"start": v(459.5, 30) * mm, "end": v(459.5, 10) * mm});
            skLineSegment(sketch, "E32.125.10.0", {"start": v(460.5, 55) * mm, "end": v(459.5, 55) * mm});
            skLineSegment(sketch, "E32.128.10.0", {"start": v(459.5, 85) * mm, "end": v(460.5, 85) * mm});
            skLineSegment(sketch, "E32.131.10.0", {"start": v(459.5, 10) * mm, "end": v(460.5, 10) * mm});
            skLineSegment(sketch, "E32.134.10.0", {"start": v(461.5, 65) * mm, "end": v(462.5, 65) * mm});
            skLineSegment(sketch, "E32.137.10.0", {"start": v(462.5, 45) * mm, "end": v(461.5, 45) * mm});
            skLineSegment(sketch, "E32.140.10.0", {"start": v(461.5, 95) * mm, "end": v(461.5, 115) * mm});
            skLineSegment(sketch, "E32.143.10.0", {"start": v(462.5, 95) * mm, "end": v(461.5, 95) * mm});
            skLineSegment(sketch, "E32.146.10.0", {"start": v(462.5, 115) * mm, "end": v(462.5, 95) * mm});
            skLineSegment(sketch, "E32.149.10.0", {"start": v(461.5, 115) * mm, "end": v(462.5, 115) * mm});
            skLineSegment(sketch, "E32.152.10.0", {"start": v(460.5, 110) * mm, "end": v(460.5, 130) * mm});
            skLineSegment(sketch, "E32.155.10.0", {"start": v(459.5, 130) * mm, "end": v(459.5, 110) * mm});
            skLineSegment(sketch, "E32.158.10.0", {"start": v(459.5, 110) * mm, "end": v(460.5, 110) * mm});
            skLineSegment(sketch, "E32.161.10.0", {"start": v(460.5, 130) * mm, "end": v(459.5, 130) * mm});
            skLineSegment(sketch, "E32.0.11.0", {"start": v(466.5, -10) * mm, "end": v(466.5, -30) * mm});
            skPoint(sketch, "E32.3.11.0", {"position": v(463.5, 95) * mm});
            skLineSegment(sketch, "E32.4.11.0", {"start": v(465.5, 70) * mm, "end": v(465.5, 90) * mm});
            skLineSegment(sketch, "E32.7.11.0", {"start": v(465.5, 45) * mm, "end": v(465.5, 65) * mm});
            skLineSegment(sketch, "E32.10.11.0", {"start": v(466.5, 65) * mm, "end": v(466.5, 45) * mm});
            skPoint(sketch, "E32.13.11.0", {"position": v(463.5, 70) * mm});
            skLineSegment(sketch, "E32.14.11.0", {"start": v(465.5, -5) * mm, "end": v(465.5, 15) * mm});
            skPoint(sketch, "E32.17.11.0", {"position": v(463.5, 20) * mm});
            skLineSegment(sketch, "E32.18.11.0", {"start": v(466.5, 40) * mm, "end": v(466.5, 20) * mm});
            skLineSegment(sketch, "E32.21.11.0", {"start": v(465.5, -30) * mm, "end": v(465.5, -10) * mm});
            skPoint(sketch, "E32.24.11.0", {"position": v(463.5, 45) * mm});
            skLineSegment(sketch, "E32.25.11.0", {"start": v(465.5, 20) * mm, "end": v(465.5, 40) * mm});
            skLineSegment(sketch, "E32.28.11.0", {"start": v(466.5, 90) * mm, "end": v(466.5, 70) * mm});
            skLineSegment(sketch, "E32.31.11.0", {"start": v(466.5, 15) * mm, "end": v(466.5, -5) * mm});
            skPoint(sketch, "E32.34.11.0", {"position": v(463.5, -5) * mm});
            skLineSegment(sketch, "E32.35.11.0", {"start": v(464.5, 85) * mm, "end": v(464.5, 105) * mm});
            skLineSegment(sketch, "E32.38.11.0", {"start": v(466.5, 95) * mm, "end": v(466.5, 70) * mm, "construction": true});
            skLineSegment(sketch, "E32.41.11.0", {"start": v(464.5, 35) * mm, "end": v(464.5, 55) * mm});
            skLineSegment(sketch, "E32.44.11.0", {"start": v(464.5, 60) * mm, "end": v(464.5, 80) * mm});
            skLineSegment(sketch, "E32.47.11.0", {"start": v(464.5, -15) * mm, "end": v(464.5, 5) * mm});
            skLineSegment(sketch, "E32.50.11.0", {"start": v(463.5, 80) * mm, "end": v(463.5, 60) * mm});
            skLineSegment(sketch, "E32.53.11.0", {"start": v(465.5, 15) * mm, "end": v(466.5, 15) * mm});
            skLineSegment(sketch, "E32.56.11.0", {"start": v(463.5, 105) * mm, "end": v(463.5, 85) * mm});
            skLineSegment(sketch, "E32.59.11.0", {"start": v(463.5, 55) * mm, "end": v(463.5, 35) * mm});
            skLineSegment(sketch, "E32.62.11.0", {"start": v(465.5, -10) * mm, "end": v(466.5, -10) * mm});
            skLineSegment(sketch, "E32.65.11.0", {"start": v(464, 55) * mm, "end": v(464, 35) * mm, "construction": true});
            skLineSegment(sketch, "E32.68.11.0", {"start": v(466.5, -5) * mm, "end": v(465.5, -5) * mm});
            skLineSegment(sketch, "E32.71.11.0", {"start": v(463.5, 5) * mm, "end": v(463.5, -15) * mm});
            skLineSegment(sketch, "E32.74.11.0", {"start": v(464, 105) * mm, "end": v(464, 85) * mm, "construction": true});
            skLineSegment(sketch, "E32.77.11.0", {"start": v(464.5, 10) * mm, "end": v(464.5, 30) * mm});
            skLineSegment(sketch, "E32.80.11.0", {"start": v(465.5, 40) * mm, "end": v(466.5, 40) * mm});
            skLineSegment(sketch, "E32.83.11.0", {"start": v(464, 80) * mm, "end": v(464, 60) * mm, "construction": true});
            skLineSegment(sketch, "E32.86.11.0", {"start": v(464, 5) * mm, "end": v(464, -15) * mm, "construction": true});
            skLineSegment(sketch, "E32.89.11.0", {"start": v(466.5, -30) * mm, "end": v(465.5, -30) * mm});
            skLineSegment(sketch, "E32.92.11.0", {"start": v(463.5, 35) * mm, "end": v(464.5, 35) * mm});
            skLineSegment(sketch, "E32.95.11.0", {"start": v(466.5, 20) * mm, "end": v(465.5, 20) * mm});
            skLineSegment(sketch, "E32.98.11.0", {"start": v(466.5, 70) * mm, "end": v(465.5, 70) * mm});
            skLineSegment(sketch, "E32.101.11.0", {"start": v(463.5, -15) * mm, "end": v(464.5, -15) * mm});
            skLineSegment(sketch, "E32.104.11.0", {"start": v(464.5, 30) * mm, "end": v(463.5, 30) * mm});
            skLineSegment(sketch, "E32.107.11.0", {"start": v(464.5, 5) * mm, "end": v(463.5, 5) * mm});
            skLineSegment(sketch, "E32.110.11.0", {"start": v(463.5, 60) * mm, "end": v(464.5, 60) * mm});
            skLineSegment(sketch, "E32.113.11.0", {"start": v(464, 30) * mm, "end": v(464, 10) * mm, "construction": true});
            skLineSegment(sketch, "E32.116.11.0", {"start": v(465.5, 90) * mm, "end": v(466.5, 90) * mm});
            skLineSegment(sketch, "E32.119.11.0", {"start": v(464.5, 80) * mm, "end": v(463.5, 80) * mm});
            skLineSegment(sketch, "E32.122.11.0", {"start": v(463.5, 30) * mm, "end": v(463.5, 10) * mm});
            skLineSegment(sketch, "E32.125.11.0", {"start": v(464.5, 55) * mm, "end": v(463.5, 55) * mm});
            skLineSegment(sketch, "E32.128.11.0", {"start": v(463.5, 85) * mm, "end": v(464.5, 85) * mm});
            skLineSegment(sketch, "E32.131.11.0", {"start": v(463.5, 10) * mm, "end": v(464.5, 10) * mm});
            skLineSegment(sketch, "E32.134.11.0", {"start": v(465.5, 65) * mm, "end": v(466.5, 65) * mm});
            skLineSegment(sketch, "E32.137.11.0", {"start": v(466.5, 45) * mm, "end": v(465.5, 45) * mm});
            skLineSegment(sketch, "E32.140.11.0", {"start": v(465.5, 95) * mm, "end": v(465.5, 115) * mm});
            skLineSegment(sketch, "E32.143.11.0", {"start": v(466.5, 95) * mm, "end": v(465.5, 95) * mm});
            skLineSegment(sketch, "E32.146.11.0", {"start": v(466.5, 115) * mm, "end": v(466.5, 95) * mm});
            skLineSegment(sketch, "E32.149.11.0", {"start": v(465.5, 115) * mm, "end": v(466.5, 115) * mm});
            skLineSegment(sketch, "E32.152.11.0", {"start": v(464.5, 110) * mm, "end": v(464.5, 130) * mm});
            skLineSegment(sketch, "E32.155.11.0", {"start": v(463.5, 130) * mm, "end": v(463.5, 110) * mm});
            skLineSegment(sketch, "E32.158.11.0", {"start": v(463.5, 110) * mm, "end": v(464.5, 110) * mm});
            skLineSegment(sketch, "E32.161.11.0", {"start": v(464.5, 130) * mm, "end": v(463.5, 130) * mm});
            skLineSegment(sketch, "E33.0.10.0", {"start": v(377.5, 90) * mm, "end": v(377.5, 70) * mm});
            skLineSegment(sketch, "E33.3.10.0", {"start": v(377.5, 115) * mm, "end": v(377.5, 95) * mm});
            skLineSegment(sketch, "E33.6.10.0", {"start": v(377.5, 65) * mm, "end": v(377.5, 45) * mm});
            skLineSegment(sketch, "E33.9.10.0", {"start": v(378.5, 70) * mm, "end": v(378.5, 90) * mm});
            skLineSegment(sketch, "E33.12.10.0", {"start": v(377.5, 15) * mm, "end": v(377.5, -5) * mm});
            skPoint(sketch, "E33.15.10.0", {"position": v(379.5, 70) * mm});
            skPoint(sketch, "E33.16.10.0", {"position": v(379.5, 120) * mm});
            skPoint(sketch, "E33.17.10.0", {"position": v(379.5, 20) * mm});
            skLineSegment(sketch, "E33.18.10.0", {"start": v(378.5, 45) * mm, "end": v(378.5, 65) * mm});
            skPoint(sketch, "E33.21.10.0", {"position": v(379.5, 95) * mm});
            skLineSegment(sketch, "E33.22.10.0", {"start": v(377.5, 40) * mm, "end": v(377.5, 20) * mm});
            skLineSegment(sketch, "E33.25.10.0", {"start": v(380.5, 110) * mm, "end": v(380.5, 130) * mm});
            skLineSegment(sketch, "E33.28.10.0", {"start": v(379.5, 130) * mm, "end": v(379.5, 110) * mm});
            skLineSegment(sketch, "E33.31.10.0", {"start": v(377.5, -10) * mm, "end": v(377.5, -30) * mm});
            skLineSegment(sketch, "E33.34.10.0", {"start": v(378.5, -5) * mm, "end": v(378.5, 15) * mm});
            skLineSegment(sketch, "E33.37.10.0", {"start": v(378.5, 95) * mm, "end": v(378.5, 115) * mm});
            skPoint(sketch, "E33.40.10.0", {"position": v(379.5, 45) * mm});
            skLineSegment(sketch, "E33.41.10.0", {"start": v(378.5, -30) * mm, "end": v(378.5, -10) * mm});
            skPoint(sketch, "E33.44.10.0", {"position": v(379.5, -5) * mm});
            skLineSegment(sketch, "E33.45.10.0", {"start": v(378.5, 20) * mm, "end": v(378.5, 40) * mm});
            skLineSegment(sketch, "E33.48.10.0", {"start": v(379.5, 105) * mm, "end": v(379.5, 85) * mm});
            skLineSegment(sketch, "E33.51.10.0", {"start": v(380.5, 60) * mm, "end": v(380.5, 80) * mm});
            skLineSegment(sketch, "E33.54.10.0", {"start": v(379.5, 80) * mm, "end": v(379.5, 60) * mm});
            skLineSegment(sketch, "E33.57.10.0", {"start": v(380.5, -15) * mm, "end": v(380.5, 5) * mm});
            skLineSegment(sketch, "E33.60.10.0", {"start": v(379.5, 5) * mm, "end": v(379.5, -15) * mm});
            skLineSegment(sketch, "E33.63.10.0", {"start": v(380.5, 85) * mm, "end": v(380.5, 105) * mm});
            skLineSegment(sketch, "E33.66.10.0", {"start": v(380, 130) * mm, "end": v(380, 110) * mm, "construction": true});
            skLineSegment(sketch, "E33.69.10.0", {"start": v(380, 105) * mm, "end": v(380, 85) * mm, "construction": true});
            skLineSegment(sketch, "E33.72.10.0", {"start": v(380.5, 10) * mm, "end": v(380.5, 30) * mm});
            skLineSegment(sketch, "E33.75.10.0", {"start": v(379.5, 55) * mm, "end": v(379.5, 35) * mm});
            skLineSegment(sketch, "E33.78.10.0", {"start": v(380, 80) * mm, "end": v(380, 60) * mm, "construction": true});
            skLineSegment(sketch, "E33.81.10.0", {"start": v(380, 5) * mm, "end": v(380, -15) * mm, "construction": true});
            skLineSegment(sketch, "E33.84.10.0", {"start": v(380.5, 35) * mm, "end": v(380.5, 55) * mm});
            skLineSegment(sketch, "E33.87.10.0", {"start": v(379.5, 30) * mm, "end": v(379.5, 10) * mm});
            skLineSegment(sketch, "E33.90.10.0", {"start": v(380.5, 80) * mm, "end": v(379.5, 80) * mm});
            skLineSegment(sketch, "E33.93.10.0", {"start": v(380, 30) * mm, "end": v(380, 10) * mm, "construction": true});
            skLineSegment(sketch, "E33.96.10.0", {"start": v(380, 55) * mm, "end": v(380, 35) * mm, "construction": true});
            skLineSegment(sketch, "E33.99.10.0", {"start": v(380.5, 5) * mm, "end": v(379.5, 5) * mm});
            skLineSegment(sketch, "E33.102.10.0", {"start": v(379.5, 85) * mm, "end": v(380.5, 85) * mm});
            skLineSegment(sketch, "E33.105.10.0", {"start": v(379.5, -15) * mm, "end": v(380.5, -15) * mm});
            skLineSegment(sketch, "E33.108.10.0", {"start": v(380.5, 105) * mm, "end": v(379.5, 105) * mm});
            skLineSegment(sketch, "E33.111.10.0", {"start": v(378.5, 115) * mm, "end": v(377.5, 115) * mm});
            skLineSegment(sketch, "E33.114.10.0", {"start": v(379.5, 35) * mm, "end": v(380.5, 35) * mm});
            skLineSegment(sketch, "E33.117.10.0", {"start": v(379.5, 10) * mm, "end": v(380.5, 10) * mm});
            skLineSegment(sketch, "E33.120.10.0", {"start": v(378.5, 15) * mm, "end": v(377.5, 15) * mm});
            skLineSegment(sketch, "E33.123.10.0", {"start": v(380.5, 55) * mm, "end": v(379.5, 55) * mm});
            skLineSegment(sketch, "E33.126.10.0", {"start": v(377.5, 20) * mm, "end": v(378.5, 20) * mm});
            skLineSegment(sketch, "E33.129.10.0", {"start": v(377.5, -5) * mm, "end": v(378.5, -5) * mm});
            skLineSegment(sketch, "E33.132.10.0", {"start": v(378.5, 90) * mm, "end": v(377.5, 90) * mm});
            skLineSegment(sketch, "E33.135.10.0", {"start": v(377.5, -30) * mm, "end": v(378.5, -30) * mm});
            skLineSegment(sketch, "E33.138.10.0", {"start": v(379.5, 60) * mm, "end": v(380.5, 60) * mm});
            skLineSegment(sketch, "E33.141.10.0", {"start": v(379.5, 110) * mm, "end": v(380.5, 110) * mm});
            skLineSegment(sketch, "E33.144.10.0", {"start": v(378.5, -10) * mm, "end": v(377.5, -10) * mm});
            skLineSegment(sketch, "E33.147.10.0", {"start": v(377.5, 45) * mm, "end": v(378.5, 45) * mm});
            skLineSegment(sketch, "E33.150.10.0", {"start": v(377.5, 95) * mm, "end": v(378.5, 95) * mm});
            skLineSegment(sketch, "E33.153.10.0", {"start": v(380.5, 30) * mm, "end": v(379.5, 30) * mm});
            skLineSegment(sketch, "E33.156.10.0", {"start": v(378.5, 40) * mm, "end": v(377.5, 40) * mm});
            skLineSegment(sketch, "E33.159.10.0", {"start": v(377.5, 70) * mm, "end": v(378.5, 70) * mm});
            skLineSegment(sketch, "E33.162.10.0", {"start": v(378.5, 65) * mm, "end": v(377.5, 65) * mm});
            skLineSegment(sketch, "E33.165.10.0", {"start": v(380.5, 130) * mm, "end": v(379.5, 130) * mm});
            skLineSegment(sketch, "E33.0.11.0", {"start": v(373.5, 90) * mm, "end": v(373.5, 70) * mm});
            skLineSegment(sketch, "E33.3.11.0", {"start": v(373.5, 115) * mm, "end": v(373.5, 95) * mm});
            skLineSegment(sketch, "E33.6.11.0", {"start": v(373.5, 65) * mm, "end": v(373.5, 45) * mm});
            skLineSegment(sketch, "E33.9.11.0", {"start": v(374.5, 70) * mm, "end": v(374.5, 90) * mm});
            skLineSegment(sketch, "E33.12.11.0", {"start": v(373.5, 15) * mm, "end": v(373.5, -5) * mm});
            skPoint(sketch, "E33.15.11.0", {"position": v(375.5, 70) * mm});
            skPoint(sketch, "E33.16.11.0", {"position": v(375.5, 120) * mm});
            skPoint(sketch, "E33.17.11.0", {"position": v(375.5, 20) * mm});
            skLineSegment(sketch, "E33.18.11.0", {"start": v(374.5, 45) * mm, "end": v(374.5, 65) * mm});
            skPoint(sketch, "E33.21.11.0", {"position": v(375.5, 95) * mm});
            skLineSegment(sketch, "E33.22.11.0", {"start": v(373.5, 40) * mm, "end": v(373.5, 20) * mm});
            skLineSegment(sketch, "E33.25.11.0", {"start": v(376.5, 110) * mm, "end": v(376.5, 130) * mm});
            skLineSegment(sketch, "E33.28.11.0", {"start": v(375.5, 130) * mm, "end": v(375.5, 110) * mm});
            skLineSegment(sketch, "E33.31.11.0", {"start": v(373.5, -10) * mm, "end": v(373.5, -30) * mm});
            skLineSegment(sketch, "E33.34.11.0", {"start": v(374.5, -5) * mm, "end": v(374.5, 15) * mm});
            skLineSegment(sketch, "E33.37.11.0", {"start": v(374.5, 95) * mm, "end": v(374.5, 115) * mm});
            skPoint(sketch, "E33.40.11.0", {"position": v(375.5, 45) * mm});
            skLineSegment(sketch, "E33.41.11.0", {"start": v(374.5, -30) * mm, "end": v(374.5, -10) * mm});
            skPoint(sketch, "E33.44.11.0", {"position": v(375.5, -5) * mm});
            skLineSegment(sketch, "E33.45.11.0", {"start": v(374.5, 20) * mm, "end": v(374.5, 40) * mm});
            skLineSegment(sketch, "E33.48.11.0", {"start": v(375.5, 105) * mm, "end": v(375.5, 85) * mm});
            skLineSegment(sketch, "E33.51.11.0", {"start": v(376.5, 60) * mm, "end": v(376.5, 80) * mm});
            skLineSegment(sketch, "E33.54.11.0", {"start": v(375.5, 80) * mm, "end": v(375.5, 60) * mm});
            skLineSegment(sketch, "E33.57.11.0", {"start": v(376.5, -15) * mm, "end": v(376.5, 5) * mm});
            skLineSegment(sketch, "E33.60.11.0", {"start": v(375.5, 5) * mm, "end": v(375.5, -15) * mm});
            skLineSegment(sketch, "E33.63.11.0", {"start": v(376.5, 85) * mm, "end": v(376.5, 105) * mm});
            skLineSegment(sketch, "E33.66.11.0", {"start": v(376, 130) * mm, "end": v(376, 110) * mm, "construction": true});
            skLineSegment(sketch, "E33.69.11.0", {"start": v(376, 105) * mm, "end": v(376, 85) * mm, "construction": true});
            skLineSegment(sketch, "E33.72.11.0", {"start": v(376.5, 10) * mm, "end": v(376.5, 30) * mm});
            skLineSegment(sketch, "E33.75.11.0", {"start": v(375.5, 55) * mm, "end": v(375.5, 35) * mm});
            skLineSegment(sketch, "E33.78.11.0", {"start": v(376, 80) * mm, "end": v(376, 60) * mm, "construction": true});
            skLineSegment(sketch, "E33.81.11.0", {"start": v(376, 5) * mm, "end": v(376, -15) * mm, "construction": true});
            skLineSegment(sketch, "E33.84.11.0", {"start": v(376.5, 35) * mm, "end": v(376.5, 55) * mm});
            skLineSegment(sketch, "E33.87.11.0", {"start": v(375.5, 30) * mm, "end": v(375.5, 10) * mm});
            skLineSegment(sketch, "E33.90.11.0", {"start": v(376.5, 80) * mm, "end": v(375.5, 80) * mm});
            skLineSegment(sketch, "E33.93.11.0", {"start": v(376, 30) * mm, "end": v(376, 10) * mm, "construction": true});
            skLineSegment(sketch, "E33.96.11.0", {"start": v(376, 55) * mm, "end": v(376, 35) * mm, "construction": true});
            skLineSegment(sketch, "E33.99.11.0", {"start": v(376.5, 5) * mm, "end": v(375.5, 5) * mm});
            skLineSegment(sketch, "E33.102.11.0", {"start": v(375.5, 85) * mm, "end": v(376.5, 85) * mm});
            skLineSegment(sketch, "E33.105.11.0", {"start": v(375.5, -15) * mm, "end": v(376.5, -15) * mm});
            skLineSegment(sketch, "E33.108.11.0", {"start": v(376.5, 105) * mm, "end": v(375.5, 105) * mm});
            skLineSegment(sketch, "E33.111.11.0", {"start": v(374.5, 115) * mm, "end": v(373.5, 115) * mm});
            skLineSegment(sketch, "E33.114.11.0", {"start": v(375.5, 35) * mm, "end": v(376.5, 35) * mm});
            skLineSegment(sketch, "E33.117.11.0", {"start": v(375.5, 10) * mm, "end": v(376.5, 10) * mm});
            skLineSegment(sketch, "E33.120.11.0", {"start": v(374.5, 15) * mm, "end": v(373.5, 15) * mm});
            skLineSegment(sketch, "E33.123.11.0", {"start": v(376.5, 55) * mm, "end": v(375.5, 55) * mm});
            skLineSegment(sketch, "E33.126.11.0", {"start": v(373.5, 20) * mm, "end": v(374.5, 20) * mm});
            skLineSegment(sketch, "E33.129.11.0", {"start": v(373.5, -5) * mm, "end": v(374.5, -5) * mm});
            skLineSegment(sketch, "E33.132.11.0", {"start": v(374.5, 90) * mm, "end": v(373.5, 90) * mm});
            skLineSegment(sketch, "E33.135.11.0", {"start": v(373.5, -30) * mm, "end": v(374.5, -30) * mm});
            skLineSegment(sketch, "E33.138.11.0", {"start": v(375.5, 60) * mm, "end": v(376.5, 60) * mm});
            skLineSegment(sketch, "E33.141.11.0", {"start": v(375.5, 110) * mm, "end": v(376.5, 110) * mm});
            skLineSegment(sketch, "E33.144.11.0", {"start": v(374.5, -10) * mm, "end": v(373.5, -10) * mm});
            skLineSegment(sketch, "E33.147.11.0", {"start": v(373.5, 45) * mm, "end": v(374.5, 45) * mm});
            skLineSegment(sketch, "E33.150.11.0", {"start": v(373.5, 95) * mm, "end": v(374.5, 95) * mm});
            skLineSegment(sketch, "E33.153.11.0", {"start": v(376.5, 30) * mm, "end": v(375.5, 30) * mm});
            skLineSegment(sketch, "E33.156.11.0", {"start": v(374.5, 40) * mm, "end": v(373.5, 40) * mm});
            skLineSegment(sketch, "E33.159.11.0", {"start": v(373.5, 70) * mm, "end": v(374.5, 70) * mm});
            skLineSegment(sketch, "E33.162.11.0", {"start": v(374.5, 65) * mm, "end": v(373.5, 65) * mm});
            skLineSegment(sketch, "E33.165.11.0", {"start": v(376.5, 130) * mm, "end": v(375.5, 130) * mm});
            skLineSegment(sketch, "E34", {"start": v(451.5, 105) * mm, "end": v(452.5, 105) * mm});
            skLineSegment(sketch, "E35", {"start": v(455.5, 105) * mm, "end": v(456.5, 105) * mm});
            skLineSegment(sketch, "E36", {"start": v(459.5, 105) * mm, "end": v(460.5, 105) * mm});
            skLineSegment(sketch, "E37", {"start": v(463.5, 105) * mm, "end": v(464.5, 105) * mm});
            const initialGuessF0  = {"E5": [0.04, 0.03, 1, 0, 0.06]};
            skSetInitialGuess(sketch, initialGuessF0);
            skSolve(sketch);
        }
        {
            assignVariable(context, id + "F1", {"name" : "MaterialThickness", "anyValue" : 3});
        }
        {
            var Q0;
            {var subQ54=sQuery(id+"F0.wireOp",EDGE,"E0");Q0=makeQuery(id+"F0.imprint","IMPRINT",FACE,{"disambiguationData":[TD([[makeQuery(id+"F0.imprint","IMPRINT",EDGE,{"derivedFrom":subQ54}),1.0]])]});}
            extrude(context, id + "F2", {"entities" : qUnion([Q0]), "depth" : (getVariable(context, 'MaterialThickness')) * mm});
        }
    });
